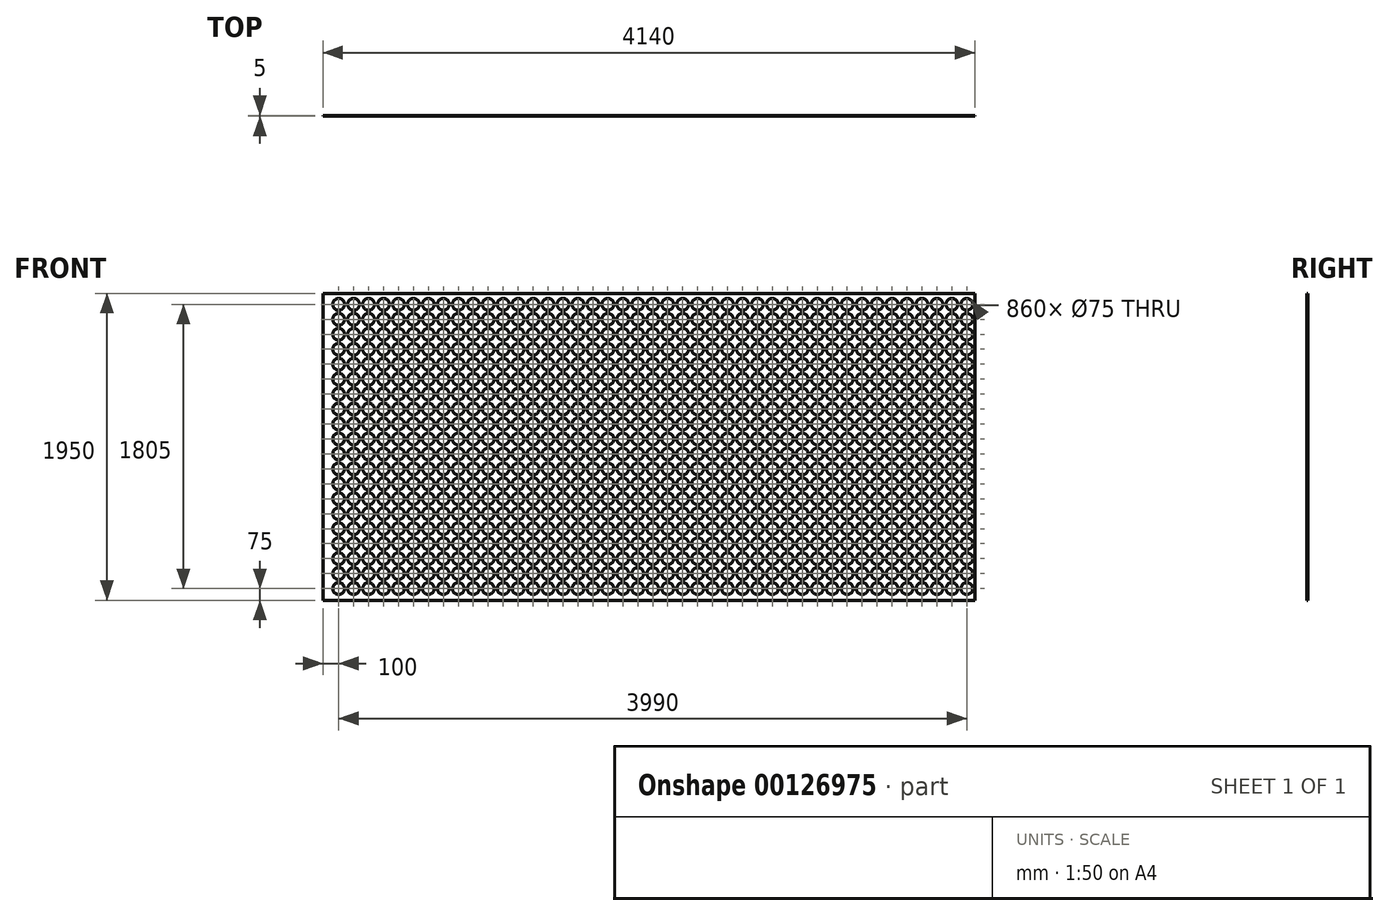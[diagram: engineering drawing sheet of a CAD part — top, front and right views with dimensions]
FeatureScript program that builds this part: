
annotation { "Feature Type Name" : "Feature", "Feature Type Description" : "" }
export const myFeature = defineFeature(function(context is Context, id is Id, definition is map)
    precondition{}
    {
        {
            var Q0;
            Q0=qCreatedBy(makeId("Front.planeOp"),FACE);
            var sketch = newSketch(context, id + "F0", { "sketchPlane" : qUnion([Q0])});
            skLineSegment(sketch, "E0.bottom", {"start": v(0, 0) * mm, "end": v(4140, 0) * mm});
            skLineSegment(sketch, "E0.top", {"start": v(0, 1950) * mm, "end": v(4140, 1950) * mm});
            skLineSegment(sketch, "E0.left", {"start": v(0, 0) * mm, "end": v(0, 1950) * mm});
            skLineSegment(sketch, "E0.right", {"start": v(4140, 0) * mm, "end": v(4140, 1950) * mm});
            skCircle(sketch, "E1", {"center": v(100, 75) * mm, "radius": 37.5 * mm});
            skCircle(sketch, "E2.0.1.0", {"center": v(100, 170) * mm, "radius": 37.5 * mm});
            skCircle(sketch, "E2.0.2.0", {"center": v(100, 265) * mm, "radius": 37.5 * mm});
            skCircle(sketch, "E2.0.3.0", {"center": v(100, 360) * mm, "radius": 37.5 * mm});
            skCircle(sketch, "E2.0.4.0", {"center": v(100, 455) * mm, "radius": 37.5 * mm});
            skCircle(sketch, "E2.0.5.0", {"center": v(100, 550) * mm, "radius": 37.5 * mm});
            skCircle(sketch, "E2.0.6.0", {"center": v(100, 645) * mm, "radius": 37.5 * mm});
            skCircle(sketch, "E2.0.7.0", {"center": v(100, 740) * mm, "radius": 37.5 * mm});
            skCircle(sketch, "E2.0.8.0", {"center": v(100, 835) * mm, "radius": 37.5 * mm});
            skCircle(sketch, "E2.0.9.0", {"center": v(100, 930) * mm, "radius": 37.5 * mm});
            skCircle(sketch, "E2.0.10.0", {"center": v(100, 1025) * mm, "radius": 37.5 * mm});
            skCircle(sketch, "E2.0.11.0", {"center": v(100, 1120) * mm, "radius": 37.5 * mm});
            skCircle(sketch, "E2.0.12.0", {"center": v(100, 1215) * mm, "radius": 37.5 * mm});
            skCircle(sketch, "E2.0.13.0", {"center": v(100, 1310) * mm, "radius": 37.5 * mm});
            skCircle(sketch, "E2.0.14.0", {"center": v(100, 1405) * mm, "radius": 37.5 * mm});
            skCircle(sketch, "E2.0.15.0", {"center": v(100, 1500) * mm, "radius": 37.5 * mm});
            skCircle(sketch, "E2.0.16.0", {"center": v(100, 1595) * mm, "radius": 37.5 * mm});
            skCircle(sketch, "E2.0.17.0", {"center": v(100, 1690) * mm, "radius": 37.5 * mm});
            skCircle(sketch, "E2.0.18.0", {"center": v(100, 1785) * mm, "radius": 37.5 * mm});
            skCircle(sketch, "E2.1.0.0", {"center": v(195, 75) * mm, "radius": 37.5 * mm});
            skCircle(sketch, "E2.1.1.0", {"center": v(195, 170) * mm, "radius": 37.5 * mm});
            skCircle(sketch, "E2.1.2.0", {"center": v(195, 265) * mm, "radius": 37.5 * mm});
            skCircle(sketch, "E2.1.3.0", {"center": v(195, 360) * mm, "radius": 37.5 * mm});
            skCircle(sketch, "E2.1.4.0", {"center": v(195, 455) * mm, "radius": 37.5 * mm});
            skCircle(sketch, "E2.1.5.0", {"center": v(195, 550) * mm, "radius": 37.5 * mm});
            skCircle(sketch, "E2.1.6.0", {"center": v(195, 645) * mm, "radius": 37.5 * mm});
            skCircle(sketch, "E2.1.7.0", {"center": v(195, 740) * mm, "radius": 37.5 * mm});
            skCircle(sketch, "E2.1.8.0", {"center": v(195, 835) * mm, "radius": 37.5 * mm});
            skCircle(sketch, "E2.1.9.0", {"center": v(195, 930) * mm, "radius": 37.5 * mm});
            skCircle(sketch, "E2.1.10.0", {"center": v(195, 1025) * mm, "radius": 37.5 * mm});
            skCircle(sketch, "E2.1.11.0", {"center": v(195, 1120) * mm, "radius": 37.5 * mm});
            skCircle(sketch, "E2.1.12.0", {"center": v(195, 1215) * mm, "radius": 37.5 * mm});
            skCircle(sketch, "E2.1.13.0", {"center": v(195, 1310) * mm, "radius": 37.5 * mm});
            skCircle(sketch, "E2.1.14.0", {"center": v(195, 1405) * mm, "radius": 37.5 * mm});
            skCircle(sketch, "E2.1.15.0", {"center": v(195, 1500) * mm, "radius": 37.5 * mm});
            skCircle(sketch, "E2.1.16.0", {"center": v(195, 1595) * mm, "radius": 37.5 * mm});
            skCircle(sketch, "E2.1.17.0", {"center": v(195, 1690) * mm, "radius": 37.5 * mm});
            skCircle(sketch, "E2.1.18.0", {"center": v(195, 1785) * mm, "radius": 37.5 * mm});
            skCircle(sketch, "E2.2.0.0", {"center": v(290, 75) * mm, "radius": 37.5 * mm});
            skCircle(sketch, "E2.2.1.0", {"center": v(290, 170) * mm, "radius": 37.5 * mm});
            skCircle(sketch, "E2.2.2.0", {"center": v(290, 265) * mm, "radius": 37.5 * mm});
            skCircle(sketch, "E2.2.3.0", {"center": v(290, 360) * mm, "radius": 37.5 * mm});
            skCircle(sketch, "E2.2.4.0", {"center": v(290, 455) * mm, "radius": 37.5 * mm});
            skCircle(sketch, "E2.2.5.0", {"center": v(290, 550) * mm, "radius": 37.5 * mm});
            skCircle(sketch, "E2.2.6.0", {"center": v(290, 645) * mm, "radius": 37.5 * mm});
            skCircle(sketch, "E2.2.7.0", {"center": v(290, 740) * mm, "radius": 37.5 * mm});
            skCircle(sketch, "E2.2.8.0", {"center": v(290, 835) * mm, "radius": 37.5 * mm});
            skCircle(sketch, "E2.2.9.0", {"center": v(290, 930) * mm, "radius": 37.5 * mm});
            skCircle(sketch, "E2.2.10.0", {"center": v(290, 1025) * mm, "radius": 37.5 * mm});
            skCircle(sketch, "E2.2.11.0", {"center": v(290, 1120) * mm, "radius": 37.5 * mm});
            skCircle(sketch, "E2.2.12.0", {"center": v(290, 1215) * mm, "radius": 37.5 * mm});
            skCircle(sketch, "E2.2.13.0", {"center": v(290, 1310) * mm, "radius": 37.5 * mm});
            skCircle(sketch, "E2.2.14.0", {"center": v(290, 1405) * mm, "radius": 37.5 * mm});
            skCircle(sketch, "E2.2.15.0", {"center": v(290, 1500) * mm, "radius": 37.5 * mm});
            skCircle(sketch, "E2.2.16.0", {"center": v(290, 1595) * mm, "radius": 37.5 * mm});
            skCircle(sketch, "E2.2.17.0", {"center": v(290, 1690) * mm, "radius": 37.5 * mm});
            skCircle(sketch, "E2.2.18.0", {"center": v(290, 1785) * mm, "radius": 37.5 * mm});
            skCircle(sketch, "E2.3.0.0", {"center": v(385, 75) * mm, "radius": 37.5 * mm});
            skCircle(sketch, "E2.3.1.0", {"center": v(385, 170) * mm, "radius": 37.5 * mm});
            skCircle(sketch, "E2.3.2.0", {"center": v(385, 265) * mm, "radius": 37.5 * mm});
            skCircle(sketch, "E2.3.3.0", {"center": v(385, 360) * mm, "radius": 37.5 * mm});
            skCircle(sketch, "E2.3.4.0", {"center": v(385, 455) * mm, "radius": 37.5 * mm});
            skCircle(sketch, "E2.3.5.0", {"center": v(385, 550) * mm, "radius": 37.5 * mm});
            skCircle(sketch, "E2.3.6.0", {"center": v(385, 645) * mm, "radius": 37.5 * mm});
            skCircle(sketch, "E2.3.7.0", {"center": v(385, 740) * mm, "radius": 37.5 * mm});
            skCircle(sketch, "E2.3.8.0", {"center": v(385, 835) * mm, "radius": 37.5 * mm});
            skCircle(sketch, "E2.3.9.0", {"center": v(385, 930) * mm, "radius": 37.5 * mm});
            skCircle(sketch, "E2.3.10.0", {"center": v(385, 1025) * mm, "radius": 37.5 * mm});
            skCircle(sketch, "E2.3.11.0", {"center": v(385, 1120) * mm, "radius": 37.5 * mm});
            skCircle(sketch, "E2.3.12.0", {"center": v(385, 1215) * mm, "radius": 37.5 * mm});
            skCircle(sketch, "E2.3.13.0", {"center": v(385, 1310) * mm, "radius": 37.5 * mm});
            skCircle(sketch, "E2.3.14.0", {"center": v(385, 1405) * mm, "radius": 37.5 * mm});
            skCircle(sketch, "E2.3.15.0", {"center": v(385, 1500) * mm, "radius": 37.5 * mm});
            skCircle(sketch, "E2.3.16.0", {"center": v(385, 1595) * mm, "radius": 37.5 * mm});
            skCircle(sketch, "E2.3.17.0", {"center": v(385, 1690) * mm, "radius": 37.5 * mm});
            skCircle(sketch, "E2.3.18.0", {"center": v(385, 1785) * mm, "radius": 37.5 * mm});
            skCircle(sketch, "E2.4.0.0", {"center": v(480, 75) * mm, "radius": 37.5 * mm});
            skCircle(sketch, "E2.4.1.0", {"center": v(480, 170) * mm, "radius": 37.5 * mm});
            skCircle(sketch, "E2.4.2.0", {"center": v(480, 265) * mm, "radius": 37.5 * mm});
            skCircle(sketch, "E2.4.3.0", {"center": v(480, 360) * mm, "radius": 37.5 * mm});
            skCircle(sketch, "E2.4.4.0", {"center": v(480, 455) * mm, "radius": 37.5 * mm});
            skCircle(sketch, "E2.4.5.0", {"center": v(480, 550) * mm, "radius": 37.5 * mm});
            skCircle(sketch, "E2.4.6.0", {"center": v(480, 645) * mm, "radius": 37.5 * mm});
            skCircle(sketch, "E2.4.7.0", {"center": v(480, 740) * mm, "radius": 37.5 * mm});
            skCircle(sketch, "E2.4.8.0", {"center": v(480, 835) * mm, "radius": 37.5 * mm});
            skCircle(sketch, "E2.4.9.0", {"center": v(480, 930) * mm, "radius": 37.5 * mm});
            skCircle(sketch, "E2.4.10.0", {"center": v(480, 1025) * mm, "radius": 37.5 * mm});
            skCircle(sketch, "E2.4.11.0", {"center": v(480, 1120) * mm, "radius": 37.5 * mm});
            skCircle(sketch, "E2.4.12.0", {"center": v(480, 1215) * mm, "radius": 37.5 * mm});
            skCircle(sketch, "E2.4.13.0", {"center": v(480, 1310) * mm, "radius": 37.5 * mm});
            skCircle(sketch, "E2.4.14.0", {"center": v(480, 1405) * mm, "radius": 37.5 * mm});
            skCircle(sketch, "E2.4.15.0", {"center": v(480, 1500) * mm, "radius": 37.5 * mm});
            skCircle(sketch, "E2.4.16.0", {"center": v(480, 1595) * mm, "radius": 37.5 * mm});
            skCircle(sketch, "E2.4.17.0", {"center": v(480, 1690) * mm, "radius": 37.5 * mm});
            skCircle(sketch, "E2.4.18.0", {"center": v(480, 1785) * mm, "radius": 37.5 * mm});
            skCircle(sketch, "E2.5.0.0", {"center": v(575, 75) * mm, "radius": 37.5 * mm});
            skCircle(sketch, "E2.5.1.0", {"center": v(575, 170) * mm, "radius": 37.5 * mm});
            skCircle(sketch, "E2.5.2.0", {"center": v(575, 265) * mm, "radius": 37.5 * mm});
            skCircle(sketch, "E2.5.3.0", {"center": v(575, 360) * mm, "radius": 37.5 * mm});
            skCircle(sketch, "E2.5.4.0", {"center": v(575, 455) * mm, "radius": 37.5 * mm});
            skCircle(sketch, "E2.5.5.0", {"center": v(575, 550) * mm, "radius": 37.5 * mm});
            skCircle(sketch, "E2.5.6.0", {"center": v(575, 645) * mm, "radius": 37.5 * mm});
            skCircle(sketch, "E2.5.7.0", {"center": v(575, 740) * mm, "radius": 37.5 * mm});
            skCircle(sketch, "E2.5.8.0", {"center": v(575, 835) * mm, "radius": 37.5 * mm});
            skCircle(sketch, "E2.5.9.0", {"center": v(575, 930) * mm, "radius": 37.5 * mm});
            skCircle(sketch, "E2.5.10.0", {"center": v(575, 1025) * mm, "radius": 37.5 * mm});
            skCircle(sketch, "E2.5.11.0", {"center": v(575, 1120) * mm, "radius": 37.5 * mm});
            skCircle(sketch, "E2.5.12.0", {"center": v(575, 1215) * mm, "radius": 37.5 * mm});
            skCircle(sketch, "E2.5.13.0", {"center": v(575, 1310) * mm, "radius": 37.5 * mm});
            skCircle(sketch, "E2.5.14.0", {"center": v(575, 1405) * mm, "radius": 37.5 * mm});
            skCircle(sketch, "E2.5.15.0", {"center": v(575, 1500) * mm, "radius": 37.5 * mm});
            skCircle(sketch, "E2.5.16.0", {"center": v(575, 1595) * mm, "radius": 37.5 * mm});
            skCircle(sketch, "E2.5.17.0", {"center": v(575, 1690) * mm, "radius": 37.5 * mm});
            skCircle(sketch, "E2.5.18.0", {"center": v(575, 1785) * mm, "radius": 37.5 * mm});
            skCircle(sketch, "E2.6.0.0", {"center": v(670, 75) * mm, "radius": 37.5 * mm});
            skCircle(sketch, "E2.6.1.0", {"center": v(670, 170) * mm, "radius": 37.5 * mm});
            skCircle(sketch, "E2.6.2.0", {"center": v(670, 265) * mm, "radius": 37.5 * mm});
            skCircle(sketch, "E2.6.3.0", {"center": v(670, 360) * mm, "radius": 37.5 * mm});
            skCircle(sketch, "E2.6.4.0", {"center": v(670, 455) * mm, "radius": 37.5 * mm});
            skCircle(sketch, "E2.6.5.0", {"center": v(670, 550) * mm, "radius": 37.5 * mm});
            skCircle(sketch, "E2.6.6.0", {"center": v(670, 645) * mm, "radius": 37.5 * mm});
            skCircle(sketch, "E2.6.7.0", {"center": v(670, 740) * mm, "radius": 37.5 * mm});
            skCircle(sketch, "E2.6.8.0", {"center": v(670, 835) * mm, "radius": 37.5 * mm});
            skCircle(sketch, "E2.6.9.0", {"center": v(670, 930) * mm, "radius": 37.5 * mm});
            skCircle(sketch, "E2.6.10.0", {"center": v(670, 1025) * mm, "radius": 37.5 * mm});
            skCircle(sketch, "E2.6.11.0", {"center": v(670, 1120) * mm, "radius": 37.5 * mm});
            skCircle(sketch, "E2.6.12.0", {"center": v(670, 1215) * mm, "radius": 37.5 * mm});
            skCircle(sketch, "E2.6.13.0", {"center": v(670, 1310) * mm, "radius": 37.5 * mm});
            skCircle(sketch, "E2.6.14.0", {"center": v(670, 1405) * mm, "radius": 37.5 * mm});
            skCircle(sketch, "E2.6.15.0", {"center": v(670, 1500) * mm, "radius": 37.5 * mm});
            skCircle(sketch, "E2.6.16.0", {"center": v(670, 1595) * mm, "radius": 37.5 * mm});
            skCircle(sketch, "E2.6.17.0", {"center": v(670, 1690) * mm, "radius": 37.5 * mm});
            skCircle(sketch, "E2.6.18.0", {"center": v(670, 1785) * mm, "radius": 37.5 * mm});
            skCircle(sketch, "E2.7.0.0", {"center": v(765, 75) * mm, "radius": 37.5 * mm});
            skCircle(sketch, "E2.7.1.0", {"center": v(765, 170) * mm, "radius": 37.5 * mm});
            skCircle(sketch, "E2.7.2.0", {"center": v(765, 265) * mm, "radius": 37.5 * mm});
            skCircle(sketch, "E2.7.3.0", {"center": v(765, 360) * mm, "radius": 37.5 * mm});
            skCircle(sketch, "E2.7.4.0", {"center": v(765, 455) * mm, "radius": 37.5 * mm});
            skCircle(sketch, "E2.7.5.0", {"center": v(765, 550) * mm, "radius": 37.5 * mm});
            skCircle(sketch, "E2.7.6.0", {"center": v(765, 645) * mm, "radius": 37.5 * mm});
            skCircle(sketch, "E2.7.7.0", {"center": v(765, 740) * mm, "radius": 37.5 * mm});
            skCircle(sketch, "E2.7.8.0", {"center": v(765, 835) * mm, "radius": 37.5 * mm});
            skCircle(sketch, "E2.7.9.0", {"center": v(765, 930) * mm, "radius": 37.5 * mm});
            skCircle(sketch, "E2.7.10.0", {"center": v(765, 1025) * mm, "radius": 37.5 * mm});
            skCircle(sketch, "E2.7.11.0", {"center": v(765, 1120) * mm, "radius": 37.5 * mm});
            skCircle(sketch, "E2.7.12.0", {"center": v(765, 1215) * mm, "radius": 37.5 * mm});
            skCircle(sketch, "E2.7.13.0", {"center": v(765, 1310) * mm, "radius": 37.5 * mm});
            skCircle(sketch, "E2.7.14.0", {"center": v(765, 1405) * mm, "radius": 37.5 * mm});
            skCircle(sketch, "E2.7.15.0", {"center": v(765, 1500) * mm, "radius": 37.5 * mm});
            skCircle(sketch, "E2.7.16.0", {"center": v(765, 1595) * mm, "radius": 37.5 * mm});
            skCircle(sketch, "E2.7.17.0", {"center": v(765, 1690) * mm, "radius": 37.5 * mm});
            skCircle(sketch, "E2.7.18.0", {"center": v(765, 1785) * mm, "radius": 37.5 * mm});
            skCircle(sketch, "E2.8.0.0", {"center": v(860, 75) * mm, "radius": 37.5 * mm});
            skCircle(sketch, "E2.8.1.0", {"center": v(860, 170) * mm, "radius": 37.5 * mm});
            skCircle(sketch, "E2.8.2.0", {"center": v(860, 265) * mm, "radius": 37.5 * mm});
            skCircle(sketch, "E2.8.3.0", {"center": v(860, 360) * mm, "radius": 37.5 * mm});
            skCircle(sketch, "E2.8.4.0", {"center": v(860, 455) * mm, "radius": 37.5 * mm});
            skCircle(sketch, "E2.8.5.0", {"center": v(860, 550) * mm, "radius": 37.5 * mm});
            skCircle(sketch, "E2.8.6.0", {"center": v(860, 645) * mm, "radius": 37.5 * mm});
            skCircle(sketch, "E2.8.7.0", {"center": v(860, 740) * mm, "radius": 37.5 * mm});
            skCircle(sketch, "E2.8.8.0", {"center": v(860, 835) * mm, "radius": 37.5 * mm});
            skCircle(sketch, "E2.8.9.0", {"center": v(860, 930) * mm, "radius": 37.5 * mm});
            skCircle(sketch, "E2.8.10.0", {"center": v(860, 1025) * mm, "radius": 37.5 * mm});
            skCircle(sketch, "E2.8.11.0", {"center": v(860, 1120) * mm, "radius": 37.5 * mm});
            skCircle(sketch, "E2.8.12.0", {"center": v(860, 1215) * mm, "radius": 37.5 * mm});
            skCircle(sketch, "E2.8.13.0", {"center": v(860, 1310) * mm, "radius": 37.5 * mm});
            skCircle(sketch, "E2.8.14.0", {"center": v(860, 1405) * mm, "radius": 37.5 * mm});
            skCircle(sketch, "E2.8.15.0", {"center": v(860, 1500) * mm, "radius": 37.5 * mm});
            skCircle(sketch, "E2.8.16.0", {"center": v(860, 1595) * mm, "radius": 37.5 * mm});
            skCircle(sketch, "E2.8.17.0", {"center": v(860, 1690) * mm, "radius": 37.5 * mm});
            skCircle(sketch, "E2.8.18.0", {"center": v(860, 1785) * mm, "radius": 37.5 * mm});
            skCircle(sketch, "E2.9.0.0", {"center": v(955, 75) * mm, "radius": 37.5 * mm});
            skCircle(sketch, "E2.9.1.0", {"center": v(955, 170) * mm, "radius": 37.5 * mm});
            skCircle(sketch, "E2.9.2.0", {"center": v(955, 265) * mm, "radius": 37.5 * mm});
            skCircle(sketch, "E2.9.3.0", {"center": v(955, 360) * mm, "radius": 37.5 * mm});
            skCircle(sketch, "E2.9.4.0", {"center": v(955, 455) * mm, "radius": 37.5 * mm});
            skCircle(sketch, "E2.9.5.0", {"center": v(955, 550) * mm, "radius": 37.5 * mm});
            skCircle(sketch, "E2.9.6.0", {"center": v(955, 645) * mm, "radius": 37.5 * mm});
            skCircle(sketch, "E2.9.7.0", {"center": v(955, 740) * mm, "radius": 37.5 * mm});
            skCircle(sketch, "E2.9.8.0", {"center": v(955, 835) * mm, "radius": 37.5 * mm});
            skCircle(sketch, "E2.9.9.0", {"center": v(955, 930) * mm, "radius": 37.5 * mm});
            skCircle(sketch, "E2.9.10.0", {"center": v(955, 1025) * mm, "radius": 37.5 * mm});
            skCircle(sketch, "E2.9.11.0", {"center": v(955, 1120) * mm, "radius": 37.5 * mm});
            skCircle(sketch, "E2.9.12.0", {"center": v(955, 1215) * mm, "radius": 37.5 * mm});
            skCircle(sketch, "E2.9.13.0", {"center": v(955, 1310) * mm, "radius": 37.5 * mm});
            skCircle(sketch, "E2.9.14.0", {"center": v(955, 1405) * mm, "radius": 37.5 * mm});
            skCircle(sketch, "E2.9.15.0", {"center": v(955, 1500) * mm, "radius": 37.5 * mm});
            skCircle(sketch, "E2.9.16.0", {"center": v(955, 1595) * mm, "radius": 37.5 * mm});
            skCircle(sketch, "E2.9.17.0", {"center": v(955, 1690) * mm, "radius": 37.5 * mm});
            skCircle(sketch, "E2.9.18.0", {"center": v(955, 1785) * mm, "radius": 37.5 * mm});
            skCircle(sketch, "E2.10.0.0", {"center": v(1050, 75) * mm, "radius": 37.5 * mm});
            skCircle(sketch, "E2.10.1.0", {"center": v(1050, 170) * mm, "radius": 37.5 * mm});
            skCircle(sketch, "E2.10.2.0", {"center": v(1050, 265) * mm, "radius": 37.5 * mm});
            skCircle(sketch, "E2.10.3.0", {"center": v(1050, 360) * mm, "radius": 37.5 * mm});
            skCircle(sketch, "E2.10.4.0", {"center": v(1050, 455) * mm, "radius": 37.5 * mm});
            skCircle(sketch, "E2.10.5.0", {"center": v(1050, 550) * mm, "radius": 37.5 * mm});
            skCircle(sketch, "E2.10.6.0", {"center": v(1050, 645) * mm, "radius": 37.5 * mm});
            skCircle(sketch, "E2.10.7.0", {"center": v(1050, 740) * mm, "radius": 37.5 * mm});
            skCircle(sketch, "E2.10.8.0", {"center": v(1050, 835) * mm, "radius": 37.5 * mm});
            skCircle(sketch, "E2.10.9.0", {"center": v(1050, 930) * mm, "radius": 37.5 * mm});
            skCircle(sketch, "E2.10.10.0", {"center": v(1050, 1025) * mm, "radius": 37.5 * mm});
            skCircle(sketch, "E2.10.11.0", {"center": v(1050, 1120) * mm, "radius": 37.5 * mm});
            skCircle(sketch, "E2.10.12.0", {"center": v(1050, 1215) * mm, "radius": 37.5 * mm});
            skCircle(sketch, "E2.10.13.0", {"center": v(1050, 1310) * mm, "radius": 37.5 * mm});
            skCircle(sketch, "E2.10.14.0", {"center": v(1050, 1405) * mm, "radius": 37.5 * mm});
            skCircle(sketch, "E2.10.15.0", {"center": v(1050, 1500) * mm, "radius": 37.5 * mm});
            skCircle(sketch, "E2.10.16.0", {"center": v(1050, 1595) * mm, "radius": 37.5 * mm});
            skCircle(sketch, "E2.10.17.0", {"center": v(1050, 1690) * mm, "radius": 37.5 * mm});
            skCircle(sketch, "E2.10.18.0", {"center": v(1050, 1785) * mm, "radius": 37.5 * mm});
            skCircle(sketch, "E2.11.0.0", {"center": v(1145, 75) * mm, "radius": 37.5 * mm});
            skCircle(sketch, "E2.11.1.0", {"center": v(1145, 170) * mm, "radius": 37.5 * mm});
            skCircle(sketch, "E2.11.2.0", {"center": v(1145, 265) * mm, "radius": 37.5 * mm});
            skCircle(sketch, "E2.11.3.0", {"center": v(1145, 360) * mm, "radius": 37.5 * mm});
            skCircle(sketch, "E2.11.4.0", {"center": v(1145, 455) * mm, "radius": 37.5 * mm});
            skCircle(sketch, "E2.11.5.0", {"center": v(1145, 550) * mm, "radius": 37.5 * mm});
            skCircle(sketch, "E2.11.6.0", {"center": v(1145, 645) * mm, "radius": 37.5 * mm});
            skCircle(sketch, "E2.11.7.0", {"center": v(1145, 740) * mm, "radius": 37.5 * mm});
            skCircle(sketch, "E2.11.8.0", {"center": v(1145, 835) * mm, "radius": 37.5 * mm});
            skCircle(sketch, "E2.11.9.0", {"center": v(1145, 930) * mm, "radius": 37.5 * mm});
            skCircle(sketch, "E2.11.10.0", {"center": v(1145, 1025) * mm, "radius": 37.5 * mm});
            skCircle(sketch, "E2.11.11.0", {"center": v(1145, 1120) * mm, "radius": 37.5 * mm});
            skCircle(sketch, "E2.11.12.0", {"center": v(1145, 1215) * mm, "radius": 37.5 * mm});
            skCircle(sketch, "E2.11.13.0", {"center": v(1145, 1310) * mm, "radius": 37.5 * mm});
            skCircle(sketch, "E2.11.14.0", {"center": v(1145, 1405) * mm, "radius": 37.5 * mm});
            skCircle(sketch, "E2.11.15.0", {"center": v(1145, 1500) * mm, "radius": 37.5 * mm});
            skCircle(sketch, "E2.11.16.0", {"center": v(1145, 1595) * mm, "radius": 37.5 * mm});
            skCircle(sketch, "E2.11.17.0", {"center": v(1145, 1690) * mm, "radius": 37.5 * mm});
            skCircle(sketch, "E2.11.18.0", {"center": v(1145, 1785) * mm, "radius": 37.5 * mm});
            skCircle(sketch, "E2.12.0.0", {"center": v(1240, 75) * mm, "radius": 37.5 * mm});
            skCircle(sketch, "E2.12.1.0", {"center": v(1240, 170) * mm, "radius": 37.5 * mm});
            skCircle(sketch, "E2.12.2.0", {"center": v(1240, 265) * mm, "radius": 37.5 * mm});
            skCircle(sketch, "E2.12.3.0", {"center": v(1240, 360) * mm, "radius": 37.5 * mm});
            skCircle(sketch, "E2.12.4.0", {"center": v(1240, 455) * mm, "radius": 37.5 * mm});
            skCircle(sketch, "E2.12.5.0", {"center": v(1240, 550) * mm, "radius": 37.5 * mm});
            skCircle(sketch, "E2.12.6.0", {"center": v(1240, 645) * mm, "radius": 37.5 * mm});
            skCircle(sketch, "E2.12.7.0", {"center": v(1240, 740) * mm, "radius": 37.5 * mm});
            skCircle(sketch, "E2.12.8.0", {"center": v(1240, 835) * mm, "radius": 37.5 * mm});
            skCircle(sketch, "E2.12.9.0", {"center": v(1240, 930) * mm, "radius": 37.5 * mm});
            skCircle(sketch, "E2.12.10.0", {"center": v(1240, 1025) * mm, "radius": 37.5 * mm});
            skCircle(sketch, "E2.12.11.0", {"center": v(1240, 1120) * mm, "radius": 37.5 * mm});
            skCircle(sketch, "E2.12.12.0", {"center": v(1240, 1215) * mm, "radius": 37.5 * mm});
            skCircle(sketch, "E2.12.13.0", {"center": v(1240, 1310) * mm, "radius": 37.5 * mm});
            skCircle(sketch, "E2.12.14.0", {"center": v(1240, 1405) * mm, "radius": 37.5 * mm});
            skCircle(sketch, "E2.12.15.0", {"center": v(1240, 1500) * mm, "radius": 37.5 * mm});
            skCircle(sketch, "E2.12.16.0", {"center": v(1240, 1595) * mm, "radius": 37.5 * mm});
            skCircle(sketch, "E2.12.17.0", {"center": v(1240, 1690) * mm, "radius": 37.5 * mm});
            skCircle(sketch, "E2.12.18.0", {"center": v(1240, 1785) * mm, "radius": 37.5 * mm});
            skCircle(sketch, "E2.13.0.0", {"center": v(1335, 75) * mm, "radius": 37.5 * mm});
            skCircle(sketch, "E2.13.1.0", {"center": v(1335, 170) * mm, "radius": 37.5 * mm});
            skCircle(sketch, "E2.13.2.0", {"center": v(1335, 265) * mm, "radius": 37.5 * mm});
            skCircle(sketch, "E2.13.3.0", {"center": v(1335, 360) * mm, "radius": 37.5 * mm});
            skCircle(sketch, "E2.13.4.0", {"center": v(1335, 455) * mm, "radius": 37.5 * mm});
            skCircle(sketch, "E2.13.5.0", {"center": v(1335, 550) * mm, "radius": 37.5 * mm});
            skCircle(sketch, "E2.13.6.0", {"center": v(1335, 645) * mm, "radius": 37.5 * mm});
            skCircle(sketch, "E2.13.7.0", {"center": v(1335, 740) * mm, "radius": 37.5 * mm});
            skCircle(sketch, "E2.13.8.0", {"center": v(1335, 835) * mm, "radius": 37.5 * mm});
            skCircle(sketch, "E2.13.9.0", {"center": v(1335, 930) * mm, "radius": 37.5 * mm});
            skCircle(sketch, "E2.13.10.0", {"center": v(1335, 1025) * mm, "radius": 37.5 * mm});
            skCircle(sketch, "E2.13.11.0", {"center": v(1335, 1120) * mm, "radius": 37.5 * mm});
            skCircle(sketch, "E2.13.12.0", {"center": v(1335, 1215) * mm, "radius": 37.5 * mm});
            skCircle(sketch, "E2.13.13.0", {"center": v(1335, 1310) * mm, "radius": 37.5 * mm});
            skCircle(sketch, "E2.13.14.0", {"center": v(1335, 1405) * mm, "radius": 37.5 * mm});
            skCircle(sketch, "E2.13.15.0", {"center": v(1335, 1500) * mm, "radius": 37.5 * mm});
            skCircle(sketch, "E2.13.16.0", {"center": v(1335, 1595) * mm, "radius": 37.5 * mm});
            skCircle(sketch, "E2.13.17.0", {"center": v(1335, 1690) * mm, "radius": 37.5 * mm});
            skCircle(sketch, "E2.13.18.0", {"center": v(1335, 1785) * mm, "radius": 37.5 * mm});
            skCircle(sketch, "E2.14.0.0", {"center": v(1430, 75) * mm, "radius": 37.5 * mm});
            skCircle(sketch, "E2.14.1.0", {"center": v(1430, 170) * mm, "radius": 37.5 * mm});
            skCircle(sketch, "E2.14.2.0", {"center": v(1430, 265) * mm, "radius": 37.5 * mm});
            skCircle(sketch, "E2.14.3.0", {"center": v(1430, 360) * mm, "radius": 37.5 * mm});
            skCircle(sketch, "E2.14.4.0", {"center": v(1430, 455) * mm, "radius": 37.5 * mm});
            skCircle(sketch, "E2.14.5.0", {"center": v(1430, 550) * mm, "radius": 37.5 * mm});
            skCircle(sketch, "E2.14.6.0", {"center": v(1430, 645) * mm, "radius": 37.5 * mm});
            skCircle(sketch, "E2.14.7.0", {"center": v(1430, 740) * mm, "radius": 37.5 * mm});
            skCircle(sketch, "E2.14.8.0", {"center": v(1430, 835) * mm, "radius": 37.5 * mm});
            skCircle(sketch, "E2.14.9.0", {"center": v(1430, 930) * mm, "radius": 37.5 * mm});
            skCircle(sketch, "E2.14.10.0", {"center": v(1430, 1025) * mm, "radius": 37.5 * mm});
            skCircle(sketch, "E2.14.11.0", {"center": v(1430, 1120) * mm, "radius": 37.5 * mm});
            skCircle(sketch, "E2.14.12.0", {"center": v(1430, 1215) * mm, "radius": 37.5 * mm});
            skCircle(sketch, "E2.14.13.0", {"center": v(1430, 1310) * mm, "radius": 37.5 * mm});
            skCircle(sketch, "E2.14.14.0", {"center": v(1430, 1405) * mm, "radius": 37.5 * mm});
            skCircle(sketch, "E2.14.15.0", {"center": v(1430, 1500) * mm, "radius": 37.5 * mm});
            skCircle(sketch, "E2.14.16.0", {"center": v(1430, 1595) * mm, "radius": 37.5 * mm});
            skCircle(sketch, "E2.14.17.0", {"center": v(1430, 1690) * mm, "radius": 37.5 * mm});
            skCircle(sketch, "E2.14.18.0", {"center": v(1430, 1785) * mm, "radius": 37.5 * mm});
            skCircle(sketch, "E2.15.0.0", {"center": v(1525, 75) * mm, "radius": 37.5 * mm});
            skCircle(sketch, "E2.15.1.0", {"center": v(1525, 170) * mm, "radius": 37.5 * mm});
            skCircle(sketch, "E2.15.2.0", {"center": v(1525, 265) * mm, "radius": 37.5 * mm});
            skCircle(sketch, "E2.15.3.0", {"center": v(1525, 360) * mm, "radius": 37.5 * mm});
            skCircle(sketch, "E2.15.4.0", {"center": v(1525, 455) * mm, "radius": 37.5 * mm});
            skCircle(sketch, "E2.15.5.0", {"center": v(1525, 550) * mm, "radius": 37.5 * mm});
            skCircle(sketch, "E2.15.6.0", {"center": v(1525, 645) * mm, "radius": 37.5 * mm});
            skCircle(sketch, "E2.15.7.0", {"center": v(1525, 740) * mm, "radius": 37.5 * mm});
            skCircle(sketch, "E2.15.8.0", {"center": v(1525, 835) * mm, "radius": 37.5 * mm});
            skCircle(sketch, "E2.15.9.0", {"center": v(1525, 930) * mm, "radius": 37.5 * mm});
            skCircle(sketch, "E2.15.10.0", {"center": v(1525, 1025) * mm, "radius": 37.5 * mm});
            skCircle(sketch, "E2.15.11.0", {"center": v(1525, 1120) * mm, "radius": 37.5 * mm});
            skCircle(sketch, "E2.15.12.0", {"center": v(1525, 1215) * mm, "radius": 37.5 * mm});
            skCircle(sketch, "E2.15.13.0", {"center": v(1525, 1310) * mm, "radius": 37.5 * mm});
            skCircle(sketch, "E2.15.14.0", {"center": v(1525, 1405) * mm, "radius": 37.5 * mm});
            skCircle(sketch, "E2.15.15.0", {"center": v(1525, 1500) * mm, "radius": 37.5 * mm});
            skCircle(sketch, "E2.15.16.0", {"center": v(1525, 1595) * mm, "radius": 37.5 * mm});
            skCircle(sketch, "E2.15.17.0", {"center": v(1525, 1690) * mm, "radius": 37.5 * mm});
            skCircle(sketch, "E2.15.18.0", {"center": v(1525, 1785) * mm, "radius": 37.5 * mm});
            skCircle(sketch, "E2.16.0.0", {"center": v(1620, 75) * mm, "radius": 37.5 * mm});
            skCircle(sketch, "E2.16.1.0", {"center": v(1620, 170) * mm, "radius": 37.5 * mm});
            skCircle(sketch, "E2.16.2.0", {"center": v(1620, 265) * mm, "radius": 37.5 * mm});
            skCircle(sketch, "E2.16.3.0", {"center": v(1620, 360) * mm, "radius": 37.5 * mm});
            skCircle(sketch, "E2.16.4.0", {"center": v(1620, 455) * mm, "radius": 37.5 * mm});
            skCircle(sketch, "E2.16.5.0", {"center": v(1620, 550) * mm, "radius": 37.5 * mm});
            skCircle(sketch, "E2.16.6.0", {"center": v(1620, 645) * mm, "radius": 37.5 * mm});
            skCircle(sketch, "E2.16.7.0", {"center": v(1620, 740) * mm, "radius": 37.5 * mm});
            skCircle(sketch, "E2.16.8.0", {"center": v(1620, 835) * mm, "radius": 37.5 * mm});
            skCircle(sketch, "E2.16.9.0", {"center": v(1620, 930) * mm, "radius": 37.5 * mm});
            skCircle(sketch, "E2.16.10.0", {"center": v(1620, 1025) * mm, "radius": 37.5 * mm});
            skCircle(sketch, "E2.16.11.0", {"center": v(1620, 1120) * mm, "radius": 37.5 * mm});
            skCircle(sketch, "E2.16.12.0", {"center": v(1620, 1215) * mm, "radius": 37.5 * mm});
            skCircle(sketch, "E2.16.13.0", {"center": v(1620, 1310) * mm, "radius": 37.5 * mm});
            skCircle(sketch, "E2.16.14.0", {"center": v(1620, 1405) * mm, "radius": 37.5 * mm});
            skCircle(sketch, "E2.16.15.0", {"center": v(1620, 1500) * mm, "radius": 37.5 * mm});
            skCircle(sketch, "E2.16.16.0", {"center": v(1620, 1595) * mm, "radius": 37.5 * mm});
            skCircle(sketch, "E2.16.17.0", {"center": v(1620, 1690) * mm, "radius": 37.5 * mm});
            skCircle(sketch, "E2.16.18.0", {"center": v(1620, 1785) * mm, "radius": 37.5 * mm});
            skCircle(sketch, "E2.17.0.0", {"center": v(1715, 75) * mm, "radius": 37.5 * mm});
            skCircle(sketch, "E2.17.1.0", {"center": v(1715, 170) * mm, "radius": 37.5 * mm});
            skCircle(sketch, "E2.17.2.0", {"center": v(1715, 265) * mm, "radius": 37.5 * mm});
            skCircle(sketch, "E2.17.3.0", {"center": v(1715, 360) * mm, "radius": 37.5 * mm});
            skCircle(sketch, "E2.17.4.0", {"center": v(1715, 455) * mm, "radius": 37.5 * mm});
            skCircle(sketch, "E2.17.5.0", {"center": v(1715, 550) * mm, "radius": 37.5 * mm});
            skCircle(sketch, "E2.17.6.0", {"center": v(1715, 645) * mm, "radius": 37.5 * mm});
            skCircle(sketch, "E2.17.7.0", {"center": v(1715, 740) * mm, "radius": 37.5 * mm});
            skCircle(sketch, "E2.17.8.0", {"center": v(1715, 835) * mm, "radius": 37.5 * mm});
            skCircle(sketch, "E2.17.9.0", {"center": v(1715, 930) * mm, "radius": 37.5 * mm});
            skCircle(sketch, "E2.17.10.0", {"center": v(1715, 1025) * mm, "radius": 37.5 * mm});
            skCircle(sketch, "E2.17.11.0", {"center": v(1715, 1120) * mm, "radius": 37.5 * mm});
            skCircle(sketch, "E2.17.12.0", {"center": v(1715, 1215) * mm, "radius": 37.5 * mm});
            skCircle(sketch, "E2.17.13.0", {"center": v(1715, 1310) * mm, "radius": 37.5 * mm});
            skCircle(sketch, "E2.17.14.0", {"center": v(1715, 1405) * mm, "radius": 37.5 * mm});
            skCircle(sketch, "E2.17.15.0", {"center": v(1715, 1500) * mm, "radius": 37.5 * mm});
            skCircle(sketch, "E2.17.16.0", {"center": v(1715, 1595) * mm, "radius": 37.5 * mm});
            skCircle(sketch, "E2.17.17.0", {"center": v(1715, 1690) * mm, "radius": 37.5 * mm});
            skCircle(sketch, "E2.17.18.0", {"center": v(1715, 1785) * mm, "radius": 37.5 * mm});
            skCircle(sketch, "E2.18.0.0", {"center": v(1810, 75) * mm, "radius": 37.5 * mm});
            skCircle(sketch, "E2.18.1.0", {"center": v(1810, 170) * mm, "radius": 37.5 * mm});
            skCircle(sketch, "E2.18.2.0", {"center": v(1810, 265) * mm, "radius": 37.5 * mm});
            skCircle(sketch, "E2.18.3.0", {"center": v(1810, 360) * mm, "radius": 37.5 * mm});
            skCircle(sketch, "E2.18.4.0", {"center": v(1810, 455) * mm, "radius": 37.5 * mm});
            skCircle(sketch, "E2.18.5.0", {"center": v(1810, 550) * mm, "radius": 37.5 * mm});
            skCircle(sketch, "E2.18.6.0", {"center": v(1810, 645) * mm, "radius": 37.5 * mm});
            skCircle(sketch, "E2.18.7.0", {"center": v(1810, 740) * mm, "radius": 37.5 * mm});
            skCircle(sketch, "E2.18.8.0", {"center": v(1810, 835) * mm, "radius": 37.5 * mm});
            skCircle(sketch, "E2.18.9.0", {"center": v(1810, 930) * mm, "radius": 37.5 * mm});
            skCircle(sketch, "E2.18.10.0", {"center": v(1810, 1025) * mm, "radius": 37.5 * mm});
            skCircle(sketch, "E2.18.11.0", {"center": v(1810, 1120) * mm, "radius": 37.5 * mm});
            skCircle(sketch, "E2.18.12.0", {"center": v(1810, 1215) * mm, "radius": 37.5 * mm});
            skCircle(sketch, "E2.18.13.0", {"center": v(1810, 1310) * mm, "radius": 37.5 * mm});
            skCircle(sketch, "E2.18.14.0", {"center": v(1810, 1405) * mm, "radius": 37.5 * mm});
            skCircle(sketch, "E2.18.15.0", {"center": v(1810, 1500) * mm, "radius": 37.5 * mm});
            skCircle(sketch, "E2.18.16.0", {"center": v(1810, 1595) * mm, "radius": 37.5 * mm});
            skCircle(sketch, "E2.18.17.0", {"center": v(1810, 1690) * mm, "radius": 37.5 * mm});
            skCircle(sketch, "E2.18.18.0", {"center": v(1810, 1785) * mm, "radius": 37.5 * mm});
            skCircle(sketch, "E2.19.0.0", {"center": v(1905, 75) * mm, "radius": 37.5 * mm});
            skCircle(sketch, "E2.19.1.0", {"center": v(1905, 170) * mm, "radius": 37.5 * mm});
            skCircle(sketch, "E2.19.2.0", {"center": v(1905, 265) * mm, "radius": 37.5 * mm});
            skCircle(sketch, "E2.19.3.0", {"center": v(1905, 360) * mm, "radius": 37.5 * mm});
            skCircle(sketch, "E2.19.4.0", {"center": v(1905, 455) * mm, "radius": 37.5 * mm});
            skCircle(sketch, "E2.19.5.0", {"center": v(1905, 550) * mm, "radius": 37.5 * mm});
            skCircle(sketch, "E2.19.6.0", {"center": v(1905, 645) * mm, "radius": 37.5 * mm});
            skCircle(sketch, "E2.19.7.0", {"center": v(1905, 740) * mm, "radius": 37.5 * mm});
            skCircle(sketch, "E2.19.8.0", {"center": v(1905, 835) * mm, "radius": 37.5 * mm});
            skCircle(sketch, "E2.19.9.0", {"center": v(1905, 930) * mm, "radius": 37.5 * mm});
            skCircle(sketch, "E2.19.10.0", {"center": v(1905, 1025) * mm, "radius": 37.5 * mm});
            skCircle(sketch, "E2.19.11.0", {"center": v(1905, 1120) * mm, "radius": 37.5 * mm});
            skCircle(sketch, "E2.19.12.0", {"center": v(1905, 1215) * mm, "radius": 37.5 * mm});
            skCircle(sketch, "E2.19.13.0", {"center": v(1905, 1310) * mm, "radius": 37.5 * mm});
            skCircle(sketch, "E2.19.14.0", {"center": v(1905, 1405) * mm, "radius": 37.5 * mm});
            skCircle(sketch, "E2.19.15.0", {"center": v(1905, 1500) * mm, "radius": 37.5 * mm});
            skCircle(sketch, "E2.19.16.0", {"center": v(1905, 1595) * mm, "radius": 37.5 * mm});
            skCircle(sketch, "E2.19.17.0", {"center": v(1905, 1690) * mm, "radius": 37.5 * mm});
            skCircle(sketch, "E2.19.18.0", {"center": v(1905, 1785) * mm, "radius": 37.5 * mm});
            skCircle(sketch, "E2.20.0.0", {"center": v(2000, 75) * mm, "radius": 37.5 * mm});
            skCircle(sketch, "E2.20.1.0", {"center": v(2000, 170) * mm, "radius": 37.5 * mm});
            skCircle(sketch, "E2.20.2.0", {"center": v(2000, 265) * mm, "radius": 37.5 * mm});
            skCircle(sketch, "E2.20.3.0", {"center": v(2000, 360) * mm, "radius": 37.5 * mm});
            skCircle(sketch, "E2.20.4.0", {"center": v(2000, 455) * mm, "radius": 37.5 * mm});
            skCircle(sketch, "E2.20.5.0", {"center": v(2000, 550) * mm, "radius": 37.5 * mm});
            skCircle(sketch, "E2.20.6.0", {"center": v(2000, 645) * mm, "radius": 37.5 * mm});
            skCircle(sketch, "E2.20.7.0", {"center": v(2000, 740) * mm, "radius": 37.5 * mm});
            skCircle(sketch, "E2.20.8.0", {"center": v(2000, 835) * mm, "radius": 37.5 * mm});
            skCircle(sketch, "E2.20.9.0", {"center": v(2000, 930) * mm, "radius": 37.5 * mm});
            skCircle(sketch, "E2.20.10.0", {"center": v(2000, 1025) * mm, "radius": 37.5 * mm});
            skCircle(sketch, "E2.20.11.0", {"center": v(2000, 1120) * mm, "radius": 37.5 * mm});
            skCircle(sketch, "E2.20.12.0", {"center": v(2000, 1215) * mm, "radius": 37.5 * mm});
            skCircle(sketch, "E2.20.13.0", {"center": v(2000, 1310) * mm, "radius": 37.5 * mm});
            skCircle(sketch, "E2.20.14.0", {"center": v(2000, 1405) * mm, "radius": 37.5 * mm});
            skCircle(sketch, "E2.20.15.0", {"center": v(2000, 1500) * mm, "radius": 37.5 * mm});
            skCircle(sketch, "E2.20.16.0", {"center": v(2000, 1595) * mm, "radius": 37.5 * mm});
            skCircle(sketch, "E2.20.17.0", {"center": v(2000, 1690) * mm, "radius": 37.5 * mm});
            skCircle(sketch, "E2.20.18.0", {"center": v(2000, 1785) * mm, "radius": 37.5 * mm});
            skCircle(sketch, "E2.21.0.0", {"center": v(2095, 75) * mm, "radius": 37.5 * mm});
            skCircle(sketch, "E2.21.1.0", {"center": v(2095, 170) * mm, "radius": 37.5 * mm});
            skCircle(sketch, "E2.21.2.0", {"center": v(2095, 265) * mm, "radius": 37.5 * mm});
            skCircle(sketch, "E2.21.3.0", {"center": v(2095, 360) * mm, "radius": 37.5 * mm});
            skCircle(sketch, "E2.21.4.0", {"center": v(2095, 455) * mm, "radius": 37.5 * mm});
            skCircle(sketch, "E2.21.5.0", {"center": v(2095, 550) * mm, "radius": 37.5 * mm});
            skCircle(sketch, "E2.21.6.0", {"center": v(2095, 645) * mm, "radius": 37.5 * mm});
            skCircle(sketch, "E2.21.7.0", {"center": v(2095, 740) * mm, "radius": 37.5 * mm});
            skCircle(sketch, "E2.21.8.0", {"center": v(2095, 835) * mm, "radius": 37.5 * mm});
            skCircle(sketch, "E2.21.9.0", {"center": v(2095, 930) * mm, "radius": 37.5 * mm});
            skCircle(sketch, "E2.21.10.0", {"center": v(2095, 1025) * mm, "radius": 37.5 * mm});
            skCircle(sketch, "E2.21.11.0", {"center": v(2095, 1120) * mm, "radius": 37.5 * mm});
            skCircle(sketch, "E2.21.12.0", {"center": v(2095, 1215) * mm, "radius": 37.5 * mm});
            skCircle(sketch, "E2.21.13.0", {"center": v(2095, 1310) * mm, "radius": 37.5 * mm});
            skCircle(sketch, "E2.21.14.0", {"center": v(2095, 1405) * mm, "radius": 37.5 * mm});
            skCircle(sketch, "E2.21.15.0", {"center": v(2095, 1500) * mm, "radius": 37.5 * mm});
            skCircle(sketch, "E2.21.16.0", {"center": v(2095, 1595) * mm, "radius": 37.5 * mm});
            skCircle(sketch, "E2.21.17.0", {"center": v(2095, 1690) * mm, "radius": 37.5 * mm});
            skCircle(sketch, "E2.21.18.0", {"center": v(2095, 1785) * mm, "radius": 37.5 * mm});
            skCircle(sketch, "E2.22.0.0", {"center": v(2190, 75) * mm, "radius": 37.5 * mm});
            skCircle(sketch, "E2.22.1.0", {"center": v(2190, 170) * mm, "radius": 37.5 * mm});
            skCircle(sketch, "E2.22.2.0", {"center": v(2190, 265) * mm, "radius": 37.5 * mm});
            skCircle(sketch, "E2.22.3.0", {"center": v(2190, 360) * mm, "radius": 37.5 * mm});
            skCircle(sketch, "E2.22.4.0", {"center": v(2190, 455) * mm, "radius": 37.5 * mm});
            skCircle(sketch, "E2.22.5.0", {"center": v(2190, 550) * mm, "radius": 37.5 * mm});
            skCircle(sketch, "E2.22.6.0", {"center": v(2190, 645) * mm, "radius": 37.5 * mm});
            skCircle(sketch, "E2.22.7.0", {"center": v(2190, 740) * mm, "radius": 37.5 * mm});
            skCircle(sketch, "E2.22.8.0", {"center": v(2190, 835) * mm, "radius": 37.5 * mm});
            skCircle(sketch, "E2.22.9.0", {"center": v(2190, 930) * mm, "radius": 37.5 * mm});
            skCircle(sketch, "E2.22.10.0", {"center": v(2190, 1025) * mm, "radius": 37.5 * mm});
            skCircle(sketch, "E2.22.11.0", {"center": v(2190, 1120) * mm, "radius": 37.5 * mm});
            skCircle(sketch, "E2.22.12.0", {"center": v(2190, 1215) * mm, "radius": 37.5 * mm});
            skCircle(sketch, "E2.22.13.0", {"center": v(2190, 1310) * mm, "radius": 37.5 * mm});
            skCircle(sketch, "E2.22.14.0", {"center": v(2190, 1405) * mm, "radius": 37.5 * mm});
            skCircle(sketch, "E2.22.15.0", {"center": v(2190, 1500) * mm, "radius": 37.5 * mm});
            skCircle(sketch, "E2.22.16.0", {"center": v(2190, 1595) * mm, "radius": 37.5 * mm});
            skCircle(sketch, "E2.22.17.0", {"center": v(2190, 1690) * mm, "radius": 37.5 * mm});
            skCircle(sketch, "E2.22.18.0", {"center": v(2190, 1785) * mm, "radius": 37.5 * mm});
            skCircle(sketch, "E2.23.0.0", {"center": v(2285, 75) * mm, "radius": 37.5 * mm});
            skCircle(sketch, "E2.23.1.0", {"center": v(2285, 170) * mm, "radius": 37.5 * mm});
            skCircle(sketch, "E2.23.2.0", {"center": v(2285, 265) * mm, "radius": 37.5 * mm});
            skCircle(sketch, "E2.23.3.0", {"center": v(2285, 360) * mm, "radius": 37.5 * mm});
            skCircle(sketch, "E2.23.4.0", {"center": v(2285, 455) * mm, "radius": 37.5 * mm});
            skCircle(sketch, "E2.23.5.0", {"center": v(2285, 550) * mm, "radius": 37.5 * mm});
            skCircle(sketch, "E2.23.6.0", {"center": v(2285, 645) * mm, "radius": 37.5 * mm});
            skCircle(sketch, "E2.23.7.0", {"center": v(2285, 740) * mm, "radius": 37.5 * mm});
            skCircle(sketch, "E2.23.8.0", {"center": v(2285, 835) * mm, "radius": 37.5 * mm});
            skCircle(sketch, "E2.23.9.0", {"center": v(2285, 930) * mm, "radius": 37.5 * mm});
            skCircle(sketch, "E2.23.10.0", {"center": v(2285, 1025) * mm, "radius": 37.5 * mm});
            skCircle(sketch, "E2.23.11.0", {"center": v(2285, 1120) * mm, "radius": 37.5 * mm});
            skCircle(sketch, "E2.23.12.0", {"center": v(2285, 1215) * mm, "radius": 37.5 * mm});
            skCircle(sketch, "E2.23.13.0", {"center": v(2285, 1310) * mm, "radius": 37.5 * mm});
            skCircle(sketch, "E2.23.14.0", {"center": v(2285, 1405) * mm, "radius": 37.5 * mm});
            skCircle(sketch, "E2.23.15.0", {"center": v(2285, 1500) * mm, "radius": 37.5 * mm});
            skCircle(sketch, "E2.23.16.0", {"center": v(2285, 1595) * mm, "radius": 37.5 * mm});
            skCircle(sketch, "E2.23.17.0", {"center": v(2285, 1690) * mm, "radius": 37.5 * mm});
            skCircle(sketch, "E2.23.18.0", {"center": v(2285, 1785) * mm, "radius": 37.5 * mm});
            skCircle(sketch, "E2.24.0.0", {"center": v(2380, 75) * mm, "radius": 37.5 * mm});
            skCircle(sketch, "E2.24.1.0", {"center": v(2380, 170) * mm, "radius": 37.5 * mm});
            skCircle(sketch, "E2.24.2.0", {"center": v(2380, 265) * mm, "radius": 37.5 * mm});
            skCircle(sketch, "E2.24.3.0", {"center": v(2380, 360) * mm, "radius": 37.5 * mm});
            skCircle(sketch, "E2.24.4.0", {"center": v(2380, 455) * mm, "radius": 37.5 * mm});
            skCircle(sketch, "E2.24.5.0", {"center": v(2380, 550) * mm, "radius": 37.5 * mm});
            skCircle(sketch, "E2.24.6.0", {"center": v(2380, 645) * mm, "radius": 37.5 * mm});
            skCircle(sketch, "E2.24.7.0", {"center": v(2380, 740) * mm, "radius": 37.5 * mm});
            skCircle(sketch, "E2.24.8.0", {"center": v(2380, 835) * mm, "radius": 37.5 * mm});
            skCircle(sketch, "E2.24.9.0", {"center": v(2380, 930) * mm, "radius": 37.5 * mm});
            skCircle(sketch, "E2.24.10.0", {"center": v(2380, 1025) * mm, "radius": 37.5 * mm});
            skCircle(sketch, "E2.24.11.0", {"center": v(2380, 1120) * mm, "radius": 37.5 * mm});
            skCircle(sketch, "E2.24.12.0", {"center": v(2380, 1215) * mm, "radius": 37.5 * mm});
            skCircle(sketch, "E2.24.13.0", {"center": v(2380, 1310) * mm, "radius": 37.5 * mm});
            skCircle(sketch, "E2.24.14.0", {"center": v(2380, 1405) * mm, "radius": 37.5 * mm});
            skCircle(sketch, "E2.24.15.0", {"center": v(2380, 1500) * mm, "radius": 37.5 * mm});
            skCircle(sketch, "E2.24.16.0", {"center": v(2380, 1595) * mm, "radius": 37.5 * mm});
            skCircle(sketch, "E2.24.17.0", {"center": v(2380, 1690) * mm, "radius": 37.5 * mm});
            skCircle(sketch, "E2.24.18.0", {"center": v(2380, 1785) * mm, "radius": 37.5 * mm});
            skCircle(sketch, "E2.25.0.0", {"center": v(2475, 75) * mm, "radius": 37.5 * mm});
            skCircle(sketch, "E2.25.1.0", {"center": v(2475, 170) * mm, "radius": 37.5 * mm});
            skCircle(sketch, "E2.25.2.0", {"center": v(2475, 265) * mm, "radius": 37.5 * mm});
            skCircle(sketch, "E2.25.3.0", {"center": v(2475, 360) * mm, "radius": 37.5 * mm});
            skCircle(sketch, "E2.25.4.0", {"center": v(2475, 455) * mm, "radius": 37.5 * mm});
            skCircle(sketch, "E2.25.5.0", {"center": v(2475, 550) * mm, "radius": 37.5 * mm});
            skCircle(sketch, "E2.25.6.0", {"center": v(2475, 645) * mm, "radius": 37.5 * mm});
            skCircle(sketch, "E2.25.7.0", {"center": v(2475, 740) * mm, "radius": 37.5 * mm});
            skCircle(sketch, "E2.25.8.0", {"center": v(2475, 835) * mm, "radius": 37.5 * mm});
            skCircle(sketch, "E2.25.9.0", {"center": v(2475, 930) * mm, "radius": 37.5 * mm});
            skCircle(sketch, "E2.25.10.0", {"center": v(2475, 1025) * mm, "radius": 37.5 * mm});
            skCircle(sketch, "E2.25.11.0", {"center": v(2475, 1120) * mm, "radius": 37.5 * mm});
            skCircle(sketch, "E2.25.12.0", {"center": v(2475, 1215) * mm, "radius": 37.5 * mm});
            skCircle(sketch, "E2.25.13.0", {"center": v(2475, 1310) * mm, "radius": 37.5 * mm});
            skCircle(sketch, "E2.25.14.0", {"center": v(2475, 1405) * mm, "radius": 37.5 * mm});
            skCircle(sketch, "E2.25.15.0", {"center": v(2475, 1500) * mm, "radius": 37.5 * mm});
            skCircle(sketch, "E2.25.16.0", {"center": v(2475, 1595) * mm, "radius": 37.5 * mm});
            skCircle(sketch, "E2.25.17.0", {"center": v(2475, 1690) * mm, "radius": 37.5 * mm});
            skCircle(sketch, "E2.25.18.0", {"center": v(2475, 1785) * mm, "radius": 37.5 * mm});
            skCircle(sketch, "E2.26.0.0", {"center": v(2570, 75) * mm, "radius": 37.5 * mm});
            skCircle(sketch, "E2.26.1.0", {"center": v(2570, 170) * mm, "radius": 37.5 * mm});
            skCircle(sketch, "E2.26.2.0", {"center": v(2570, 265) * mm, "radius": 37.5 * mm});
            skCircle(sketch, "E2.26.3.0", {"center": v(2570, 360) * mm, "radius": 37.5 * mm});
            skCircle(sketch, "E2.26.4.0", {"center": v(2570, 455) * mm, "radius": 37.5 * mm});
            skCircle(sketch, "E2.26.5.0", {"center": v(2570, 550) * mm, "radius": 37.5 * mm});
            skCircle(sketch, "E2.26.6.0", {"center": v(2570, 645) * mm, "radius": 37.5 * mm});
            skCircle(sketch, "E2.26.7.0", {"center": v(2570, 740) * mm, "radius": 37.5 * mm});
            skCircle(sketch, "E2.26.8.0", {"center": v(2570, 835) * mm, "radius": 37.5 * mm});
            skCircle(sketch, "E2.26.9.0", {"center": v(2570, 930) * mm, "radius": 37.5 * mm});
            skCircle(sketch, "E2.26.10.0", {"center": v(2570, 1025) * mm, "radius": 37.5 * mm});
            skCircle(sketch, "E2.26.11.0", {"center": v(2570, 1120) * mm, "radius": 37.5 * mm});
            skCircle(sketch, "E2.26.12.0", {"center": v(2570, 1215) * mm, "radius": 37.5 * mm});
            skCircle(sketch, "E2.26.13.0", {"center": v(2570, 1310) * mm, "radius": 37.5 * mm});
            skCircle(sketch, "E2.26.14.0", {"center": v(2570, 1405) * mm, "radius": 37.5 * mm});
            skCircle(sketch, "E2.26.15.0", {"center": v(2570, 1500) * mm, "radius": 37.5 * mm});
            skCircle(sketch, "E2.26.16.0", {"center": v(2570, 1595) * mm, "radius": 37.5 * mm});
            skCircle(sketch, "E2.26.17.0", {"center": v(2570, 1690) * mm, "radius": 37.5 * mm});
            skCircle(sketch, "E2.26.18.0", {"center": v(2570, 1785) * mm, "radius": 37.5 * mm});
            skCircle(sketch, "E2.27.0.0", {"center": v(2665, 75) * mm, "radius": 37.5 * mm});
            skCircle(sketch, "E2.27.1.0", {"center": v(2665, 170) * mm, "radius": 37.5 * mm});
            skCircle(sketch, "E2.27.2.0", {"center": v(2665, 265) * mm, "radius": 37.5 * mm});
            skCircle(sketch, "E2.27.3.0", {"center": v(2665, 360) * mm, "radius": 37.5 * mm});
            skCircle(sketch, "E2.27.4.0", {"center": v(2665, 455) * mm, "radius": 37.5 * mm});
            skCircle(sketch, "E2.27.5.0", {"center": v(2665, 550) * mm, "radius": 37.5 * mm});
            skCircle(sketch, "E2.27.6.0", {"center": v(2665, 645) * mm, "radius": 37.5 * mm});
            skCircle(sketch, "E2.27.7.0", {"center": v(2665, 740) * mm, "radius": 37.5 * mm});
            skCircle(sketch, "E2.27.8.0", {"center": v(2665, 835) * mm, "radius": 37.5 * mm});
            skCircle(sketch, "E2.27.9.0", {"center": v(2665, 930) * mm, "radius": 37.5 * mm});
            skCircle(sketch, "E2.27.10.0", {"center": v(2665, 1025) * mm, "radius": 37.5 * mm});
            skCircle(sketch, "E2.27.11.0", {"center": v(2665, 1120) * mm, "radius": 37.5 * mm});
            skCircle(sketch, "E2.27.12.0", {"center": v(2665, 1215) * mm, "radius": 37.5 * mm});
            skCircle(sketch, "E2.27.13.0", {"center": v(2665, 1310) * mm, "radius": 37.5 * mm});
            skCircle(sketch, "E2.27.14.0", {"center": v(2665, 1405) * mm, "radius": 37.5 * mm});
            skCircle(sketch, "E2.27.15.0", {"center": v(2665, 1500) * mm, "radius": 37.5 * mm});
            skCircle(sketch, "E2.27.16.0", {"center": v(2665, 1595) * mm, "radius": 37.5 * mm});
            skCircle(sketch, "E2.27.17.0", {"center": v(2665, 1690) * mm, "radius": 37.5 * mm});
            skCircle(sketch, "E2.27.18.0", {"center": v(2665, 1785) * mm, "radius": 37.5 * mm});
            skCircle(sketch, "E2.28.0.0", {"center": v(2760, 75) * mm, "radius": 37.5 * mm});
            skCircle(sketch, "E2.28.1.0", {"center": v(2760, 170) * mm, "radius": 37.5 * mm});
            skCircle(sketch, "E2.28.2.0", {"center": v(2760, 265) * mm, "radius": 37.5 * mm});
            skCircle(sketch, "E2.28.3.0", {"center": v(2760, 360) * mm, "radius": 37.5 * mm});
            skCircle(sketch, "E2.28.4.0", {"center": v(2760, 455) * mm, "radius": 37.5 * mm});
            skCircle(sketch, "E2.28.5.0", {"center": v(2760, 550) * mm, "radius": 37.5 * mm});
            skCircle(sketch, "E2.28.6.0", {"center": v(2760, 645) * mm, "radius": 37.5 * mm});
            skCircle(sketch, "E2.28.7.0", {"center": v(2760, 740) * mm, "radius": 37.5 * mm});
            skCircle(sketch, "E2.28.8.0", {"center": v(2760, 835) * mm, "radius": 37.5 * mm});
            skCircle(sketch, "E2.28.9.0", {"center": v(2760, 930) * mm, "radius": 37.5 * mm});
            skCircle(sketch, "E2.28.10.0", {"center": v(2760, 1025) * mm, "radius": 37.5 * mm});
            skCircle(sketch, "E2.28.11.0", {"center": v(2760, 1120) * mm, "radius": 37.5 * mm});
            skCircle(sketch, "E2.28.12.0", {"center": v(2760, 1215) * mm, "radius": 37.5 * mm});
            skCircle(sketch, "E2.28.13.0", {"center": v(2760, 1310) * mm, "radius": 37.5 * mm});
            skCircle(sketch, "E2.28.14.0", {"center": v(2760, 1405) * mm, "radius": 37.5 * mm});
            skCircle(sketch, "E2.28.15.0", {"center": v(2760, 1500) * mm, "radius": 37.5 * mm});
            skCircle(sketch, "E2.28.16.0", {"center": v(2760, 1595) * mm, "radius": 37.5 * mm});
            skCircle(sketch, "E2.28.17.0", {"center": v(2760, 1690) * mm, "radius": 37.5 * mm});
            skCircle(sketch, "E2.28.18.0", {"center": v(2760, 1785) * mm, "radius": 37.5 * mm});
            skCircle(sketch, "E2.29.0.0", {"center": v(2855, 75) * mm, "radius": 37.5 * mm});
            skCircle(sketch, "E2.29.1.0", {"center": v(2855, 170) * mm, "radius": 37.5 * mm});
            skCircle(sketch, "E2.29.2.0", {"center": v(2855, 265) * mm, "radius": 37.5 * mm});
            skCircle(sketch, "E2.29.3.0", {"center": v(2855, 360) * mm, "radius": 37.5 * mm});
            skCircle(sketch, "E2.29.4.0", {"center": v(2855, 455) * mm, "radius": 37.5 * mm});
            skCircle(sketch, "E2.29.5.0", {"center": v(2855, 550) * mm, "radius": 37.5 * mm});
            skCircle(sketch, "E2.29.6.0", {"center": v(2855, 645) * mm, "radius": 37.5 * mm});
            skCircle(sketch, "E2.29.7.0", {"center": v(2855, 740) * mm, "radius": 37.5 * mm});
            skCircle(sketch, "E2.29.8.0", {"center": v(2855, 835) * mm, "radius": 37.5 * mm});
            skCircle(sketch, "E2.29.9.0", {"center": v(2855, 930) * mm, "radius": 37.5 * mm});
            skCircle(sketch, "E2.29.10.0", {"center": v(2855, 1025) * mm, "radius": 37.5 * mm});
            skCircle(sketch, "E2.29.11.0", {"center": v(2855, 1120) * mm, "radius": 37.5 * mm});
            skCircle(sketch, "E2.29.12.0", {"center": v(2855, 1215) * mm, "radius": 37.5 * mm});
            skCircle(sketch, "E2.29.13.0", {"center": v(2855, 1310) * mm, "radius": 37.5 * mm});
            skCircle(sketch, "E2.29.14.0", {"center": v(2855, 1405) * mm, "radius": 37.5 * mm});
            skCircle(sketch, "E2.29.15.0", {"center": v(2855, 1500) * mm, "radius": 37.5 * mm});
            skCircle(sketch, "E2.29.16.0", {"center": v(2855, 1595) * mm, "radius": 37.5 * mm});
            skCircle(sketch, "E2.29.17.0", {"center": v(2855, 1690) * mm, "radius": 37.5 * mm});
            skCircle(sketch, "E2.29.18.0", {"center": v(2855, 1785) * mm, "radius": 37.5 * mm});
            skCircle(sketch, "E2.30.0.0", {"center": v(2950, 75) * mm, "radius": 37.5 * mm});
            skCircle(sketch, "E2.30.1.0", {"center": v(2950, 170) * mm, "radius": 37.5 * mm});
            skCircle(sketch, "E2.30.2.0", {"center": v(2950, 265) * mm, "radius": 37.5 * mm});
            skCircle(sketch, "E2.30.3.0", {"center": v(2950, 360) * mm, "radius": 37.5 * mm});
            skCircle(sketch, "E2.30.4.0", {"center": v(2950, 455) * mm, "radius": 37.5 * mm});
            skCircle(sketch, "E2.30.5.0", {"center": v(2950, 550) * mm, "radius": 37.5 * mm});
            skCircle(sketch, "E2.30.6.0", {"center": v(2950, 645) * mm, "radius": 37.5 * mm});
            skCircle(sketch, "E2.30.7.0", {"center": v(2950, 740) * mm, "radius": 37.5 * mm});
            skCircle(sketch, "E2.30.8.0", {"center": v(2950, 835) * mm, "radius": 37.5 * mm});
            skCircle(sketch, "E2.30.9.0", {"center": v(2950, 930) * mm, "radius": 37.5 * mm});
            skCircle(sketch, "E2.30.10.0", {"center": v(2950, 1025) * mm, "radius": 37.5 * mm});
            skCircle(sketch, "E2.30.11.0", {"center": v(2950, 1120) * mm, "radius": 37.5 * mm});
            skCircle(sketch, "E2.30.12.0", {"center": v(2950, 1215) * mm, "radius": 37.5 * mm});
            skCircle(sketch, "E2.30.13.0", {"center": v(2950, 1310) * mm, "radius": 37.5 * mm});
            skCircle(sketch, "E2.30.14.0", {"center": v(2950, 1405) * mm, "radius": 37.5 * mm});
            skCircle(sketch, "E2.30.15.0", {"center": v(2950, 1500) * mm, "radius": 37.5 * mm});
            skCircle(sketch, "E2.30.16.0", {"center": v(2950, 1595) * mm, "radius": 37.5 * mm});
            skCircle(sketch, "E2.30.17.0", {"center": v(2950, 1690) * mm, "radius": 37.5 * mm});
            skCircle(sketch, "E2.30.18.0", {"center": v(2950, 1785) * mm, "radius": 37.5 * mm});
            skCircle(sketch, "E2.31.0.0", {"center": v(3045, 75) * mm, "radius": 37.5 * mm});
            skCircle(sketch, "E2.31.1.0", {"center": v(3045, 170) * mm, "radius": 37.5 * mm});
            skCircle(sketch, "E2.31.2.0", {"center": v(3045, 265) * mm, "radius": 37.5 * mm});
            skCircle(sketch, "E2.31.3.0", {"center": v(3045, 360) * mm, "radius": 37.5 * mm});
            skCircle(sketch, "E2.31.4.0", {"center": v(3045, 455) * mm, "radius": 37.5 * mm});
            skCircle(sketch, "E2.31.5.0", {"center": v(3045, 550) * mm, "radius": 37.5 * mm});
            skCircle(sketch, "E2.31.6.0", {"center": v(3045, 645) * mm, "radius": 37.5 * mm});
            skCircle(sketch, "E2.31.7.0", {"center": v(3045, 740) * mm, "radius": 37.5 * mm});
            skCircle(sketch, "E2.31.8.0", {"center": v(3045, 835) * mm, "radius": 37.5 * mm});
            skCircle(sketch, "E2.31.9.0", {"center": v(3045, 930) * mm, "radius": 37.5 * mm});
            skCircle(sketch, "E2.31.10.0", {"center": v(3045, 1025) * mm, "radius": 37.5 * mm});
            skCircle(sketch, "E2.31.11.0", {"center": v(3045, 1120) * mm, "radius": 37.5 * mm});
            skCircle(sketch, "E2.31.12.0", {"center": v(3045, 1215) * mm, "radius": 37.5 * mm});
            skCircle(sketch, "E2.31.13.0", {"center": v(3045, 1310) * mm, "radius": 37.5 * mm});
            skCircle(sketch, "E2.31.14.0", {"center": v(3045, 1405) * mm, "radius": 37.5 * mm});
            skCircle(sketch, "E2.31.15.0", {"center": v(3045, 1500) * mm, "radius": 37.5 * mm});
            skCircle(sketch, "E2.31.16.0", {"center": v(3045, 1595) * mm, "radius": 37.5 * mm});
            skCircle(sketch, "E2.31.17.0", {"center": v(3045, 1690) * mm, "radius": 37.5 * mm});
            skCircle(sketch, "E2.31.18.0", {"center": v(3045, 1785) * mm, "radius": 37.5 * mm});
            skCircle(sketch, "E2.32.0.0", {"center": v(3140, 75) * mm, "radius": 37.5 * mm});
            skCircle(sketch, "E2.32.1.0", {"center": v(3140, 170) * mm, "radius": 37.5 * mm});
            skCircle(sketch, "E2.32.2.0", {"center": v(3140, 265) * mm, "radius": 37.5 * mm});
            skCircle(sketch, "E2.32.3.0", {"center": v(3140, 360) * mm, "radius": 37.5 * mm});
            skCircle(sketch, "E2.32.4.0", {"center": v(3140, 455) * mm, "radius": 37.5 * mm});
            skCircle(sketch, "E2.32.5.0", {"center": v(3140, 550) * mm, "radius": 37.5 * mm});
            skCircle(sketch, "E2.32.6.0", {"center": v(3140, 645) * mm, "radius": 37.5 * mm});
            skCircle(sketch, "E2.32.7.0", {"center": v(3140, 740) * mm, "radius": 37.5 * mm});
            skCircle(sketch, "E2.32.8.0", {"center": v(3140, 835) * mm, "radius": 37.5 * mm});
            skCircle(sketch, "E2.32.9.0", {"center": v(3140, 930) * mm, "radius": 37.5 * mm});
            skCircle(sketch, "E2.32.10.0", {"center": v(3140, 1025) * mm, "radius": 37.5 * mm});
            skCircle(sketch, "E2.32.11.0", {"center": v(3140, 1120) * mm, "radius": 37.5 * mm});
            skCircle(sketch, "E2.32.12.0", {"center": v(3140, 1215) * mm, "radius": 37.5 * mm});
            skCircle(sketch, "E2.32.13.0", {"center": v(3140, 1310) * mm, "radius": 37.5 * mm});
            skCircle(sketch, "E2.32.14.0", {"center": v(3140, 1405) * mm, "radius": 37.5 * mm});
            skCircle(sketch, "E2.32.15.0", {"center": v(3140, 1500) * mm, "radius": 37.5 * mm});
            skCircle(sketch, "E2.32.16.0", {"center": v(3140, 1595) * mm, "radius": 37.5 * mm});
            skCircle(sketch, "E2.32.17.0", {"center": v(3140, 1690) * mm, "radius": 37.5 * mm});
            skCircle(sketch, "E2.32.18.0", {"center": v(3140, 1785) * mm, "radius": 37.5 * mm});
            skCircle(sketch, "E2.33.0.0", {"center": v(3235, 75) * mm, "radius": 37.5 * mm});
            skCircle(sketch, "E2.33.1.0", {"center": v(3235, 170) * mm, "radius": 37.5 * mm});
            skCircle(sketch, "E2.33.2.0", {"center": v(3235, 265) * mm, "radius": 37.5 * mm});
            skCircle(sketch, "E2.33.3.0", {"center": v(3235, 360) * mm, "radius": 37.5 * mm});
            skCircle(sketch, "E2.33.4.0", {"center": v(3235, 455) * mm, "radius": 37.5 * mm});
            skCircle(sketch, "E2.33.5.0", {"center": v(3235, 550) * mm, "radius": 37.5 * mm});
            skCircle(sketch, "E2.33.6.0", {"center": v(3235, 645) * mm, "radius": 37.5 * mm});
            skCircle(sketch, "E2.33.7.0", {"center": v(3235, 740) * mm, "radius": 37.5 * mm});
            skCircle(sketch, "E2.33.8.0", {"center": v(3235, 835) * mm, "radius": 37.5 * mm});
            skCircle(sketch, "E2.33.9.0", {"center": v(3235, 930) * mm, "radius": 37.5 * mm});
            skCircle(sketch, "E2.33.10.0", {"center": v(3235, 1025) * mm, "radius": 37.5 * mm});
            skCircle(sketch, "E2.33.11.0", {"center": v(3235, 1120) * mm, "radius": 37.5 * mm});
            skCircle(sketch, "E2.33.12.0", {"center": v(3235, 1215) * mm, "radius": 37.5 * mm});
            skCircle(sketch, "E2.33.13.0", {"center": v(3235, 1310) * mm, "radius": 37.5 * mm});
            skCircle(sketch, "E2.33.14.0", {"center": v(3235, 1405) * mm, "radius": 37.5 * mm});
            skCircle(sketch, "E2.33.15.0", {"center": v(3235, 1500) * mm, "radius": 37.5 * mm});
            skCircle(sketch, "E2.33.16.0", {"center": v(3235, 1595) * mm, "radius": 37.5 * mm});
            skCircle(sketch, "E2.33.17.0", {"center": v(3235, 1690) * mm, "radius": 37.5 * mm});
            skCircle(sketch, "E2.33.18.0", {"center": v(3235, 1785) * mm, "radius": 37.5 * mm});
            skCircle(sketch, "E2.34.0.0", {"center": v(3330, 75) * mm, "radius": 37.5 * mm});
            skCircle(sketch, "E2.34.1.0", {"center": v(3330, 170) * mm, "radius": 37.5 * mm});
            skCircle(sketch, "E2.34.2.0", {"center": v(3330, 265) * mm, "radius": 37.5 * mm});
            skCircle(sketch, "E2.34.3.0", {"center": v(3330, 360) * mm, "radius": 37.5 * mm});
            skCircle(sketch, "E2.34.4.0", {"center": v(3330, 455) * mm, "radius": 37.5 * mm});
            skCircle(sketch, "E2.34.5.0", {"center": v(3330, 550) * mm, "radius": 37.5 * mm});
            skCircle(sketch, "E2.34.6.0", {"center": v(3330, 645) * mm, "radius": 37.5 * mm});
            skCircle(sketch, "E2.34.7.0", {"center": v(3330, 740) * mm, "radius": 37.5 * mm});
            skCircle(sketch, "E2.34.8.0", {"center": v(3330, 835) * mm, "radius": 37.5 * mm});
            skCircle(sketch, "E2.34.9.0", {"center": v(3330, 930) * mm, "radius": 37.5 * mm});
            skCircle(sketch, "E2.34.10.0", {"center": v(3330, 1025) * mm, "radius": 37.5 * mm});
            skCircle(sketch, "E2.34.11.0", {"center": v(3330, 1120) * mm, "radius": 37.5 * mm});
            skCircle(sketch, "E2.34.12.0", {"center": v(3330, 1215) * mm, "radius": 37.5 * mm});
            skCircle(sketch, "E2.34.13.0", {"center": v(3330, 1310) * mm, "radius": 37.5 * mm});
            skCircle(sketch, "E2.34.14.0", {"center": v(3330, 1405) * mm, "radius": 37.5 * mm});
            skCircle(sketch, "E2.34.15.0", {"center": v(3330, 1500) * mm, "radius": 37.5 * mm});
            skCircle(sketch, "E2.34.16.0", {"center": v(3330, 1595) * mm, "radius": 37.5 * mm});
            skCircle(sketch, "E2.34.17.0", {"center": v(3330, 1690) * mm, "radius": 37.5 * mm});
            skCircle(sketch, "E2.34.18.0", {"center": v(3330, 1785) * mm, "radius": 37.5 * mm});
            skCircle(sketch, "E2.35.0.0", {"center": v(3425, 75) * mm, "radius": 37.5 * mm});
            skCircle(sketch, "E2.35.1.0", {"center": v(3425, 170) * mm, "radius": 37.5 * mm});
            skCircle(sketch, "E2.35.2.0", {"center": v(3425, 265) * mm, "radius": 37.5 * mm});
            skCircle(sketch, "E2.35.3.0", {"center": v(3425, 360) * mm, "radius": 37.5 * mm});
            skCircle(sketch, "E2.35.4.0", {"center": v(3425, 455) * mm, "radius": 37.5 * mm});
            skCircle(sketch, "E2.35.5.0", {"center": v(3425, 550) * mm, "radius": 37.5 * mm});
            skCircle(sketch, "E2.35.6.0", {"center": v(3425, 645) * mm, "radius": 37.5 * mm});
            skCircle(sketch, "E2.35.7.0", {"center": v(3425, 740) * mm, "radius": 37.5 * mm});
            skCircle(sketch, "E2.35.8.0", {"center": v(3425, 835) * mm, "radius": 37.5 * mm});
            skCircle(sketch, "E2.35.9.0", {"center": v(3425, 930) * mm, "radius": 37.5 * mm});
            skCircle(sketch, "E2.35.10.0", {"center": v(3425, 1025) * mm, "radius": 37.5 * mm});
            skCircle(sketch, "E2.35.11.0", {"center": v(3425, 1120) * mm, "radius": 37.5 * mm});
            skCircle(sketch, "E2.35.12.0", {"center": v(3425, 1215) * mm, "radius": 37.5 * mm});
            skCircle(sketch, "E2.35.13.0", {"center": v(3425, 1310) * mm, "radius": 37.5 * mm});
            skCircle(sketch, "E2.35.14.0", {"center": v(3425, 1405) * mm, "radius": 37.5 * mm});
            skCircle(sketch, "E2.35.15.0", {"center": v(3425, 1500) * mm, "radius": 37.5 * mm});
            skCircle(sketch, "E2.35.16.0", {"center": v(3425, 1595) * mm, "radius": 37.5 * mm});
            skCircle(sketch, "E2.35.17.0", {"center": v(3425, 1690) * mm, "radius": 37.5 * mm});
            skCircle(sketch, "E2.35.18.0", {"center": v(3425, 1785) * mm, "radius": 37.5 * mm});
            skCircle(sketch, "E2.36.0.0", {"center": v(3520, 75) * mm, "radius": 37.5 * mm});
            skCircle(sketch, "E2.36.1.0", {"center": v(3520, 170) * mm, "radius": 37.5 * mm});
            skCircle(sketch, "E2.36.2.0", {"center": v(3520, 265) * mm, "radius": 37.5 * mm});
            skCircle(sketch, "E2.36.3.0", {"center": v(3520, 360) * mm, "radius": 37.5 * mm});
            skCircle(sketch, "E2.36.4.0", {"center": v(3520, 455) * mm, "radius": 37.5 * mm});
            skCircle(sketch, "E2.36.5.0", {"center": v(3520, 550) * mm, "radius": 37.5 * mm});
            skCircle(sketch, "E2.36.6.0", {"center": v(3520, 645) * mm, "radius": 37.5 * mm});
            skCircle(sketch, "E2.36.7.0", {"center": v(3520, 740) * mm, "radius": 37.5 * mm});
            skCircle(sketch, "E2.36.8.0", {"center": v(3520, 835) * mm, "radius": 37.5 * mm});
            skCircle(sketch, "E2.36.9.0", {"center": v(3520, 930) * mm, "radius": 37.5 * mm});
            skCircle(sketch, "E2.36.10.0", {"center": v(3520, 1025) * mm, "radius": 37.5 * mm});
            skCircle(sketch, "E2.36.11.0", {"center": v(3520, 1120) * mm, "radius": 37.5 * mm});
            skCircle(sketch, "E2.36.12.0", {"center": v(3520, 1215) * mm, "radius": 37.5 * mm});
            skCircle(sketch, "E2.36.13.0", {"center": v(3520, 1310) * mm, "radius": 37.5 * mm});
            skCircle(sketch, "E2.36.14.0", {"center": v(3520, 1405) * mm, "radius": 37.5 * mm});
            skCircle(sketch, "E2.36.15.0", {"center": v(3520, 1500) * mm, "radius": 37.5 * mm});
            skCircle(sketch, "E2.36.16.0", {"center": v(3520, 1595) * mm, "radius": 37.5 * mm});
            skCircle(sketch, "E2.36.17.0", {"center": v(3520, 1690) * mm, "radius": 37.5 * mm});
            skCircle(sketch, "E2.36.18.0", {"center": v(3520, 1785) * mm, "radius": 37.5 * mm});
            skCircle(sketch, "E2.37.0.0", {"center": v(3615, 75) * mm, "radius": 37.5 * mm});
            skCircle(sketch, "E2.37.1.0", {"center": v(3615, 170) * mm, "radius": 37.5 * mm});
            skCircle(sketch, "E2.37.2.0", {"center": v(3615, 265) * mm, "radius": 37.5 * mm});
            skCircle(sketch, "E2.37.3.0", {"center": v(3615, 360) * mm, "radius": 37.5 * mm});
            skCircle(sketch, "E2.37.4.0", {"center": v(3615, 455) * mm, "radius": 37.5 * mm});
            skCircle(sketch, "E2.37.5.0", {"center": v(3615, 550) * mm, "radius": 37.5 * mm});
            skCircle(sketch, "E2.37.6.0", {"center": v(3615, 645) * mm, "radius": 37.5 * mm});
            skCircle(sketch, "E2.37.7.0", {"center": v(3615, 740) * mm, "radius": 37.5 * mm});
            skCircle(sketch, "E2.37.8.0", {"center": v(3615, 835) * mm, "radius": 37.5 * mm});
            skCircle(sketch, "E2.37.9.0", {"center": v(3615, 930) * mm, "radius": 37.5 * mm});
            skCircle(sketch, "E2.37.10.0", {"center": v(3615, 1025) * mm, "radius": 37.5 * mm});
            skCircle(sketch, "E2.37.11.0", {"center": v(3615, 1120) * mm, "radius": 37.5 * mm});
            skCircle(sketch, "E2.37.12.0", {"center": v(3615, 1215) * mm, "radius": 37.5 * mm});
            skCircle(sketch, "E2.37.13.0", {"center": v(3615, 1310) * mm, "radius": 37.5 * mm});
            skCircle(sketch, "E2.37.14.0", {"center": v(3615, 1405) * mm, "radius": 37.5 * mm});
            skCircle(sketch, "E2.37.15.0", {"center": v(3615, 1500) * mm, "radius": 37.5 * mm});
            skCircle(sketch, "E2.37.16.0", {"center": v(3615, 1595) * mm, "radius": 37.5 * mm});
            skCircle(sketch, "E2.37.17.0", {"center": v(3615, 1690) * mm, "radius": 37.5 * mm});
            skCircle(sketch, "E2.37.18.0", {"center": v(3615, 1785) * mm, "radius": 37.5 * mm});
            skCircle(sketch, "E2.38.0.0", {"center": v(3710, 75) * mm, "radius": 37.5 * mm});
            skCircle(sketch, "E2.38.1.0", {"center": v(3710, 170) * mm, "radius": 37.5 * mm});
            skCircle(sketch, "E2.38.2.0", {"center": v(3710, 265) * mm, "radius": 37.5 * mm});
            skCircle(sketch, "E2.38.3.0", {"center": v(3710, 360) * mm, "radius": 37.5 * mm});
            skCircle(sketch, "E2.38.4.0", {"center": v(3710, 455) * mm, "radius": 37.5 * mm});
            skCircle(sketch, "E2.38.5.0", {"center": v(3710, 550) * mm, "radius": 37.5 * mm});
            skCircle(sketch, "E2.38.6.0", {"center": v(3710, 645) * mm, "radius": 37.5 * mm});
            skCircle(sketch, "E2.38.7.0", {"center": v(3710, 740) * mm, "radius": 37.5 * mm});
            skCircle(sketch, "E2.38.8.0", {"center": v(3710, 835) * mm, "radius": 37.5 * mm});
            skCircle(sketch, "E2.38.9.0", {"center": v(3710, 930) * mm, "radius": 37.5 * mm});
            skCircle(sketch, "E2.38.10.0", {"center": v(3710, 1025) * mm, "radius": 37.5 * mm});
            skCircle(sketch, "E2.38.11.0", {"center": v(3710, 1120) * mm, "radius": 37.5 * mm});
            skCircle(sketch, "E2.38.12.0", {"center": v(3710, 1215) * mm, "radius": 37.5 * mm});
            skCircle(sketch, "E2.38.13.0", {"center": v(3710, 1310) * mm, "radius": 37.5 * mm});
            skCircle(sketch, "E2.38.14.0", {"center": v(3710, 1405) * mm, "radius": 37.5 * mm});
            skCircle(sketch, "E2.38.15.0", {"center": v(3710, 1500) * mm, "radius": 37.5 * mm});
            skCircle(sketch, "E2.38.16.0", {"center": v(3710, 1595) * mm, "radius": 37.5 * mm});
            skCircle(sketch, "E2.38.17.0", {"center": v(3710, 1690) * mm, "radius": 37.5 * mm});
            skCircle(sketch, "E2.38.18.0", {"center": v(3710, 1785) * mm, "radius": 37.5 * mm});
            skCircle(sketch, "E2.39.0.0", {"center": v(3805, 75) * mm, "radius": 37.5 * mm});
            skCircle(sketch, "E2.39.1.0", {"center": v(3805, 170) * mm, "radius": 37.5 * mm});
            skCircle(sketch, "E2.39.2.0", {"center": v(3805, 265) * mm, "radius": 37.5 * mm});
            skCircle(sketch, "E2.39.3.0", {"center": v(3805, 360) * mm, "radius": 37.5 * mm});
            skCircle(sketch, "E2.39.4.0", {"center": v(3805, 455) * mm, "radius": 37.5 * mm});
            skCircle(sketch, "E2.39.5.0", {"center": v(3805, 550) * mm, "radius": 37.5 * mm});
            skCircle(sketch, "E2.39.6.0", {"center": v(3805, 645) * mm, "radius": 37.5 * mm});
            skCircle(sketch, "E2.39.7.0", {"center": v(3805, 740) * mm, "radius": 37.5 * mm});
            skCircle(sketch, "E2.39.8.0", {"center": v(3805, 835) * mm, "radius": 37.5 * mm});
            skCircle(sketch, "E2.39.9.0", {"center": v(3805, 930) * mm, "radius": 37.5 * mm});
            skCircle(sketch, "E2.39.10.0", {"center": v(3805, 1025) * mm, "radius": 37.5 * mm});
            skCircle(sketch, "E2.39.11.0", {"center": v(3805, 1120) * mm, "radius": 37.5 * mm});
            skCircle(sketch, "E2.39.12.0", {"center": v(3805, 1215) * mm, "radius": 37.5 * mm});
            skCircle(sketch, "E2.39.13.0", {"center": v(3805, 1310) * mm, "radius": 37.5 * mm});
            skCircle(sketch, "E2.39.14.0", {"center": v(3805, 1405) * mm, "radius": 37.5 * mm});
            skCircle(sketch, "E2.39.15.0", {"center": v(3805, 1500) * mm, "radius": 37.5 * mm});
            skCircle(sketch, "E2.39.16.0", {"center": v(3805, 1595) * mm, "radius": 37.5 * mm});
            skCircle(sketch, "E2.39.17.0", {"center": v(3805, 1690) * mm, "radius": 37.5 * mm});
            skCircle(sketch, "E2.39.18.0", {"center": v(3805, 1785) * mm, "radius": 37.5 * mm});
            skCircle(sketch, "E2.40.0.0", {"center": v(3900, 75) * mm, "radius": 37.5 * mm});
            skCircle(sketch, "E2.40.1.0", {"center": v(3900, 170) * mm, "radius": 37.5 * mm});
            skCircle(sketch, "E2.40.2.0", {"center": v(3900, 265) * mm, "radius": 37.5 * mm});
            skCircle(sketch, "E2.40.3.0", {"center": v(3900, 360) * mm, "radius": 37.5 * mm});
            skCircle(sketch, "E2.40.4.0", {"center": v(3900, 455) * mm, "radius": 37.5 * mm});
            skCircle(sketch, "E2.40.5.0", {"center": v(3900, 550) * mm, "radius": 37.5 * mm});
            skCircle(sketch, "E2.40.6.0", {"center": v(3900, 645) * mm, "radius": 37.5 * mm});
            skCircle(sketch, "E2.40.7.0", {"center": v(3900, 740) * mm, "radius": 37.5 * mm});
            skCircle(sketch, "E2.40.8.0", {"center": v(3900, 835) * mm, "radius": 37.5 * mm});
            skCircle(sketch, "E2.40.9.0", {"center": v(3900, 930) * mm, "radius": 37.5 * mm});
            skCircle(sketch, "E2.40.10.0", {"center": v(3900, 1025) * mm, "radius": 37.5 * mm});
            skCircle(sketch, "E2.40.11.0", {"center": v(3900, 1120) * mm, "radius": 37.5 * mm});
            skCircle(sketch, "E2.40.12.0", {"center": v(3900, 1215) * mm, "radius": 37.5 * mm});
            skCircle(sketch, "E2.40.13.0", {"center": v(3900, 1310) * mm, "radius": 37.5 * mm});
            skCircle(sketch, "E2.40.14.0", {"center": v(3900, 1405) * mm, "radius": 37.5 * mm});
            skCircle(sketch, "E2.40.15.0", {"center": v(3900, 1500) * mm, "radius": 37.5 * mm});
            skCircle(sketch, "E2.40.16.0", {"center": v(3900, 1595) * mm, "radius": 37.5 * mm});
            skCircle(sketch, "E2.40.17.0", {"center": v(3900, 1690) * mm, "radius": 37.5 * mm});
            skCircle(sketch, "E2.40.18.0", {"center": v(3900, 1785) * mm, "radius": 37.5 * mm});
            skCircle(sketch, "E2.41.0.0", {"center": v(3995, 75) * mm, "radius": 37.5 * mm});
            skCircle(sketch, "E2.41.1.0", {"center": v(3995, 170) * mm, "radius": 37.5 * mm});
            skCircle(sketch, "E2.41.2.0", {"center": v(3995, 265) * mm, "radius": 37.5 * mm});
            skCircle(sketch, "E2.41.3.0", {"center": v(3995, 360) * mm, "radius": 37.5 * mm});
            skCircle(sketch, "E2.41.4.0", {"center": v(3995, 455) * mm, "radius": 37.5 * mm});
            skCircle(sketch, "E2.41.5.0", {"center": v(3995, 550) * mm, "radius": 37.5 * mm});
            skCircle(sketch, "E2.41.6.0", {"center": v(3995, 645) * mm, "radius": 37.5 * mm});
            skCircle(sketch, "E2.41.7.0", {"center": v(3995, 740) * mm, "radius": 37.5 * mm});
            skCircle(sketch, "E2.41.8.0", {"center": v(3995, 835) * mm, "radius": 37.5 * mm});
            skCircle(sketch, "E2.41.9.0", {"center": v(3995, 930) * mm, "radius": 37.5 * mm});
            skCircle(sketch, "E2.41.10.0", {"center": v(3995, 1025) * mm, "radius": 37.5 * mm});
            skCircle(sketch, "E2.41.11.0", {"center": v(3995, 1120) * mm, "radius": 37.5 * mm});
            skCircle(sketch, "E2.41.12.0", {"center": v(3995, 1215) * mm, "radius": 37.5 * mm});
            skCircle(sketch, "E2.41.13.0", {"center": v(3995, 1310) * mm, "radius": 37.5 * mm});
            skCircle(sketch, "E2.41.14.0", {"center": v(3995, 1405) * mm, "radius": 37.5 * mm});
            skCircle(sketch, "E2.41.15.0", {"center": v(3995, 1500) * mm, "radius": 37.5 * mm});
            skCircle(sketch, "E2.41.16.0", {"center": v(3995, 1595) * mm, "radius": 37.5 * mm});
            skCircle(sketch, "E2.41.17.0", {"center": v(3995, 1690) * mm, "radius": 37.5 * mm});
            skCircle(sketch, "E2.41.18.0", {"center": v(3995, 1785) * mm, "radius": 37.5 * mm});
            skCircle(sketch, "E2.42.0.0", {"center": v(4090, 75) * mm, "radius": 37.5 * mm});
            skCircle(sketch, "E2.42.1.0", {"center": v(4090, 170) * mm, "radius": 37.5 * mm});
            skCircle(sketch, "E2.42.2.0", {"center": v(4090, 265) * mm, "radius": 37.5 * mm});
            skCircle(sketch, "E2.42.3.0", {"center": v(4090, 360) * mm, "radius": 37.5 * mm});
            skCircle(sketch, "E2.42.4.0", {"center": v(4090, 455) * mm, "radius": 37.5 * mm});
            skCircle(sketch, "E2.42.5.0", {"center": v(4090, 550) * mm, "radius": 37.5 * mm});
            skCircle(sketch, "E2.42.6.0", {"center": v(4090, 645) * mm, "radius": 37.5 * mm});
            skCircle(sketch, "E2.42.7.0", {"center": v(4090, 740) * mm, "radius": 37.5 * mm});
            skCircle(sketch, "E2.42.8.0", {"center": v(4090, 835) * mm, "radius": 37.5 * mm});
            skCircle(sketch, "E2.42.9.0", {"center": v(4090, 930) * mm, "radius": 37.5 * mm});
            skCircle(sketch, "E2.42.10.0", {"center": v(4090, 1025) * mm, "radius": 37.5 * mm});
            skCircle(sketch, "E2.42.11.0", {"center": v(4090, 1120) * mm, "radius": 37.5 * mm});
            skCircle(sketch, "E2.42.12.0", {"center": v(4090, 1215) * mm, "radius": 37.5 * mm});
            skCircle(sketch, "E2.42.13.0", {"center": v(4090, 1310) * mm, "radius": 37.5 * mm});
            skCircle(sketch, "E2.42.14.0", {"center": v(4090, 1405) * mm, "radius": 37.5 * mm});
            skCircle(sketch, "E2.42.15.0", {"center": v(4090, 1500) * mm, "radius": 37.5 * mm});
            skCircle(sketch, "E2.42.16.0", {"center": v(4090, 1595) * mm, "radius": 37.5 * mm});
            skCircle(sketch, "E2.42.17.0", {"center": v(4090, 1690) * mm, "radius": 37.5 * mm});
            skCircle(sketch, "E2.42.18.0", {"center": v(4090, 1785) * mm, "radius": 37.5 * mm});
            skLineSegment(sketch, "E2.direction1", {"start": v(75, 75) * mm, "end": v(170, 75) * mm, "construction": true});
            skLineSegment(sketch, "E2.direction2", {"start": v(75, 75) * mm, "end": v(75, 170) * mm, "construction": true});
            skCircle(sketch, "E3.0.0.19", {"center": v(100, 1880) * mm, "radius": 37.5 * mm});
            skCircle(sketch, "E3.0.1.19", {"center": v(195, 1880) * mm, "radius": 37.5 * mm});
            skCircle(sketch, "E3.0.2.19", {"center": v(290, 1880) * mm, "radius": 37.5 * mm});
            skCircle(sketch, "E3.0.3.19", {"center": v(385, 1880) * mm, "radius": 37.5 * mm});
            skCircle(sketch, "E3.0.4.19", {"center": v(480, 1880) * mm, "radius": 37.5 * mm});
            skCircle(sketch, "E3.0.5.19", {"center": v(575, 1880) * mm, "radius": 37.5 * mm});
            skCircle(sketch, "E3.0.6.19", {"center": v(670, 1880) * mm, "radius": 37.5 * mm});
            skCircle(sketch, "E3.0.7.19", {"center": v(765, 1880) * mm, "radius": 37.5 * mm});
            skCircle(sketch, "E3.0.8.19", {"center": v(860, 1880) * mm, "radius": 37.5 * mm});
            skCircle(sketch, "E3.0.9.19", {"center": v(955, 1880) * mm, "radius": 37.5 * mm});
            skCircle(sketch, "E3.0.10.19", {"center": v(1050, 1880) * mm, "radius": 37.5 * mm});
            skCircle(sketch, "E3.0.11.19", {"center": v(1145, 1880) * mm, "radius": 37.5 * mm});
            skCircle(sketch, "E3.0.12.19", {"center": v(1240, 1880) * mm, "radius": 37.5 * mm});
            skCircle(sketch, "E3.0.13.19", {"center": v(1335, 1880) * mm, "radius": 37.5 * mm});
            skCircle(sketch, "E3.0.14.19", {"center": v(1430, 1880) * mm, "radius": 37.5 * mm});
            skCircle(sketch, "E3.0.15.19", {"center": v(1525, 1880) * mm, "radius": 37.5 * mm});
            skCircle(sketch, "E3.0.16.19", {"center": v(1620, 1880) * mm, "radius": 37.5 * mm});
            skCircle(sketch, "E3.0.17.19", {"center": v(1715, 1880) * mm, "radius": 37.5 * mm});
            skCircle(sketch, "E3.0.18.19", {"center": v(1810, 1880) * mm, "radius": 37.5 * mm});
            skCircle(sketch, "E3.0.19.19", {"center": v(1905, 1880) * mm, "radius": 37.5 * mm});
            skCircle(sketch, "E3.0.20.19", {"center": v(2000, 1880) * mm, "radius": 37.5 * mm});
            skCircle(sketch, "E3.0.21.19", {"center": v(2095, 1880) * mm, "radius": 37.5 * mm});
            skCircle(sketch, "E3.0.22.19", {"center": v(2190, 1880) * mm, "radius": 37.5 * mm});
            skCircle(sketch, "E3.0.23.19", {"center": v(2285, 1880) * mm, "radius": 37.5 * mm});
            skCircle(sketch, "E3.0.24.19", {"center": v(2380, 1880) * mm, "radius": 37.5 * mm});
            skCircle(sketch, "E3.0.25.19", {"center": v(2475, 1880) * mm, "radius": 37.5 * mm});
            skCircle(sketch, "E3.0.26.19", {"center": v(2570, 1880) * mm, "radius": 37.5 * mm});
            skCircle(sketch, "E3.0.27.19", {"center": v(2665, 1880) * mm, "radius": 37.5 * mm});
            skCircle(sketch, "E3.0.28.19", {"center": v(2760, 1880) * mm, "radius": 37.5 * mm});
            skCircle(sketch, "E3.0.29.19", {"center": v(2855, 1880) * mm, "radius": 37.5 * mm});
            skCircle(sketch, "E3.0.30.19", {"center": v(2950, 1880) * mm, "radius": 37.5 * mm});
            skCircle(sketch, "E3.0.31.19", {"center": v(3045, 1880) * mm, "radius": 37.5 * mm});
            skCircle(sketch, "E3.0.32.19", {"center": v(3140, 1880) * mm, "radius": 37.5 * mm});
            skCircle(sketch, "E3.0.33.19", {"center": v(3235, 1880) * mm, "radius": 37.5 * mm});
            skCircle(sketch, "E3.0.34.19", {"center": v(3330, 1880) * mm, "radius": 37.5 * mm});
            skCircle(sketch, "E3.0.35.19", {"center": v(3425, 1880) * mm, "radius": 37.5 * mm});
            skCircle(sketch, "E3.0.36.19", {"center": v(3520, 1880) * mm, "radius": 37.5 * mm});
            skCircle(sketch, "E3.0.37.19", {"center": v(3615, 1880) * mm, "radius": 37.5 * mm});
            skCircle(sketch, "E3.0.38.19", {"center": v(3710, 1880) * mm, "radius": 37.5 * mm});
            skCircle(sketch, "E3.0.39.19", {"center": v(3805, 1880) * mm, "radius": 37.5 * mm});
            skCircle(sketch, "E3.0.40.19", {"center": v(3900, 1880) * mm, "radius": 37.5 * mm});
            skCircle(sketch, "E3.0.41.19", {"center": v(3995, 1880) * mm, "radius": 37.5 * mm});
            skCircle(sketch, "E3.0.42.19", {"center": v(4090, 1880) * mm, "radius": 37.5 * mm});
            skSolve(sketch);
        }
        {
            var Q0;
            Q0 = qSketchRegion(id + "F0", true);
            var Q1;
            Q1=makeQuery(id+"F0.imprint","IMPRINT",FACE,{"disambiguationData":[TD([[makeQuery(id+"F0.imprint","IMPRINT",EDGE,{"derivedFrom":sQuery(id+"F0.wireOp",EDGE,"E0.bottom")}),1.0]])]});
            extrude(context, id + "F1", {"entities" : qUnion([Q0, Q1]), "depth" : 5 * mm});
        }
    });
